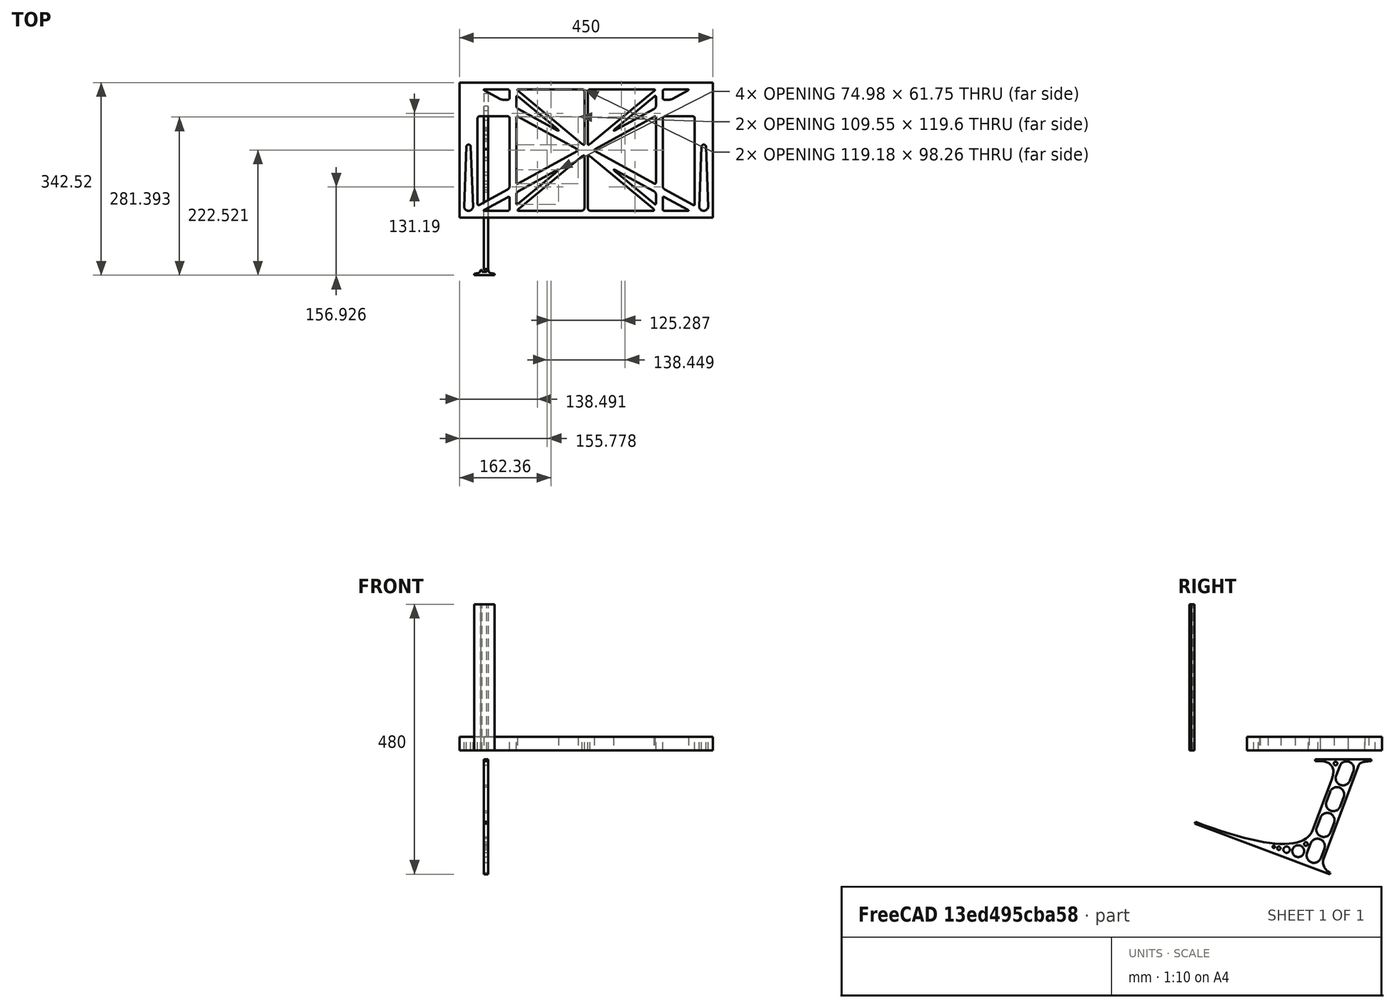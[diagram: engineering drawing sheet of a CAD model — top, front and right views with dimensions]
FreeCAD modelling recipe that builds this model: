
FCSTD DOCUMENT  (FreeCAD 0.19R0.19.2)
Label: laptopStand158FCStd
License: All rights reserved
LicenseURL: http://en.wikipedia.org/wiki/All_rights_reserved
objects: Sketcher::SketchObject×4, Part::Extrusion×3
note: 7 computed .brp shape members not serialized (recipe doc carries the construction recipe); baked Part::Feature solids carry a one-line shape summary decoded from their .brp

FEATURE [Sketcher::SketchObject] Sketch
  FullyConstrained = false
  sketch-geometry (349):
    g0: LineSegment StartX=-10.9272 StartY=-82.7794 StartZ=0 EndX=46.0728 EndY=-51.4823 EndZ=0
    g1: LineSegment StartX=-10.9272 StartY=76.4095 StartZ=0 EndX=-10.9272 EndY=-82.7794 EndZ=0
    g2: LineSegment StartX=46.0728 StartY=76.4095 StartZ=0 EndX=46.0728 EndY=-51.4823 EndZ=0
    g3: LineSegment StartX=-42.9272 StartY=136.221 StartZ=0 EndX=-42.9272 EndY=-103.779 EndZ=0
    g4: LineSegment StartX=407.073 StartY=136.221 StartZ=0 EndX=407.073 EndY=-103.779 EndZ=0
    g5: ArcOfCircle CenterX=-26.9272 CenterY=-83.7794 CenterZ=0 NormalX=0 NormalY=0 NormalZ=1 AngleXU=0 Radius=8 StartAngle=3.14159 EndAngle=6.28319
    g6: ArcOfCircle CenterX=391.073 CenterY=22.1087 CenterZ=0 NormalX=0 NormalY=0 NormalZ=1 AngleXU=0 Radius=8 StartAngle=-4.4e-15 EndAngle=3.14159
    g7: LineSegment StartX=399.073 StartY=22.1087 StartZ=0 EndX=399.073 EndY=-83.7794 EndZ=0
    g8: LineSegment StartX=383.073 StartY=22.1087 StartZ=0 EndX=383.073 EndY=-83.7794 EndZ=0
    g9: ArcOfCircle CenterX=391.073 CenterY=-83.7794 CenterZ=0 NormalX=0 NormalY=0 NormalZ=1 AngleXU=0 Radius=8 StartAngle=3.14159 EndAngle=6.28319
    g10: Circle CenterX=175.022 CenterY=27.0628 CenterZ=0 NormalX=0 NormalY=0 NormalZ=1 AngleXU=0 Radius=1
    g11: Circle CenterX=179.022 CenterY=24.8665 CenterZ=0 NormalX=0 NormalY=0 NormalZ=1 AngleXU=0 Radius=1
    g12: Circle CenterX=179.022 CenterY=27.0628 CenterZ=0 NormalX=0 NormalY=0 NormalZ=1 AngleXU=0 Radius=1
    g13: BSplineCurve PolesCount=3 KnotsCount=2 Degree=2 IsPeriodic=0
    g14: GeomPoint X=175.022 Y=27.0628 Z=0
    g15: GeomPoint X=179.022 Y=27.0628 Z=0
    g16: Circle CenterX=189.124 CenterY=27.0628 CenterZ=0 NormalX=0 NormalY=0 NormalZ=1 AngleXU=0 Radius=1
    g17: Circle CenterX=185.124 CenterY=24.8665 CenterZ=0 NormalX=0 NormalY=0 NormalZ=1 AngleXU=0 Radius=1
    g18: Circle CenterX=185.124 CenterY=27.0628 CenterZ=0 NormalX=0 NormalY=0 NormalZ=1 AngleXU=0 Radius=1
    g19: BSplineCurve PolesCount=3 KnotsCount=2 Degree=2 IsPeriodic=0
    g20: GeomPoint X=189.124 Y=27.0628 Z=0
    g21: GeomPoint X=185.124 Y=27.0628 Z=0
    g22: Circle CenterX=175.022 CenterY=5.37834 CenterZ=0 NormalX=0 NormalY=0 NormalZ=1 AngleXU=0 Radius=1
    g23: Circle CenterX=179.022 CenterY=7.57463 CenterZ=0 NormalX=0 NormalY=0 NormalZ=1 AngleXU=0 Radius=1
    g24: Circle CenterX=179.022 CenterY=5.34704 CenterZ=0 NormalX=0 NormalY=0 NormalZ=1 AngleXU=0 Radius=1
    g25: BSplineCurve PolesCount=3 KnotsCount=2 Degree=2 IsPeriodic=0
    g26: GeomPoint X=175.022 Y=5.37834 Z=0
    g27: GeomPoint X=179.022 Y=5.34704 Z=0
    g28: Circle CenterX=189.124 CenterY=5.37834 CenterZ=0 NormalX=0 NormalY=0 NormalZ=1 AngleXU=0 Radius=1
    g29: Circle CenterX=185.124 CenterY=7.57463 CenterZ=0 NormalX=0 NormalY=0 NormalZ=1 AngleXU=0 Radius=1
    g30: Circle CenterX=185.124 CenterY=5.34704 CenterZ=0 NormalX=0 NormalY=0 NormalZ=1 AngleXU=0 Radius=1
    g31: BSplineCurve PolesCount=3 KnotsCount=2 Degree=2 IsPeriodic=0
    g32: GeomPoint X=189.124 Y=5.37834 Z=0
    g33: GeomPoint X=185.124 Y=5.34704 Z=0
    g34: Circle CenterX=165.871 CenterY=18.1458 CenterZ=0 NormalX=0 NormalY=0 NormalZ=1 AngleXU=0 Radius=1
    g35: Circle CenterX=169.377 CenterY=16.2206 CenterZ=0 NormalX=0 NormalY=0 NormalZ=1 AngleXU=0 Radius=1
    g36: Circle CenterX=165.871 CenterY=14.2954 CenterZ=0 NormalX=0 NormalY=0 NormalZ=1 AngleXU=0 Radius=1
    g37: BSplineCurve PolesCount=3 KnotsCount=2 Degree=2 IsPeriodic=0
    g38: GeomPoint X=165.871 Y=18.1458 Z=0
    g39: GeomPoint X=165.871 Y=14.2954 Z=0
    g40: Circle CenterX=198.275 CenterY=18.1458 CenterZ=0 NormalX=0 NormalY=0 NormalZ=1 AngleXU=0 Radius=1
    g41: Circle CenterX=194.768 CenterY=16.2206 CenterZ=0 NormalX=0 NormalY=0 NormalZ=1 AngleXU=0 Radius=1
    g42: Circle CenterX=198.275 CenterY=14.2954 CenterZ=0 NormalX=0 NormalY=0 NormalZ=1 AngleXU=0 Radius=1
    g43: BSplineCurve PolesCount=3 KnotsCount=2 Degree=2 IsPeriodic=0
    g44: GeomPoint X=198.275 Y=18.1458 Z=0
    g45: GeomPoint X=198.275 Y=14.2954 Z=0
    g46: LineSegment StartX=407.073 StartY=-103.779 StartZ=0 EndX=-42.9272 EndY=-103.779 EndZ=0
    g47: LineSegment StartX=407.073 StartY=136.221 StartZ=0 EndX=-42.9272 EndY=136.221 EndZ=0
    g48: LineSegment StartX=46.0728 StartY=76.4095 StartZ=0 EndX=-10.9272 EndY=76.4095 EndZ=0
    g49: Circle CenterX=125.607 CenterY=54.1951 CenterZ=0 NormalX=0 NormalY=0 NormalZ=1 AngleXU=0 Radius=1
    g50: Circle CenterX=139.632 CenterY=46.4944 CenterZ=0 NormalX=0 NormalY=0 NormalZ=1 AngleXU=0 Radius=1
    g51: Circle CenterX=127.326 CenterY=56.7187 CenterZ=0 NormalX=0 NormalY=0 NormalZ=1 AngleXU=0 Radius=1
    g52: BSplineCurve PolesCount=3 KnotsCount=2 Degree=2 IsPeriodic=0
    g53: GeomPoint X=125.607 Y=54.1951 Z=0
    g54: GeomPoint X=127.326 Y=56.7187 Z=0
    g55: Circle CenterX=236.821 CenterY=56.7187 CenterZ=0 NormalX=0 NormalY=0 NormalZ=1 AngleXU=0 Radius=1
    g56: Circle CenterX=224.513 CenterY=46.4944 CenterZ=0 NormalX=0 NormalY=0 NormalZ=1 AngleXU=0 Radius=1
    g57: Circle CenterX=238.538 CenterY=54.1951 CenterZ=0 NormalX=0 NormalY=0 NormalZ=1 AngleXU=0 Radius=1
    g58: BSplineCurve PolesCount=3 KnotsCount=2 Degree=2 IsPeriodic=0
    g59: GeomPoint X=236.821 Y=56.7187 Z=0
    g60: GeomPoint X=238.538 Y=54.1951 Z=0
    g61: Circle CenterX=238.538 CenterY=-21.7539 CenterZ=0 NormalX=0 NormalY=0 NormalZ=1 AngleXU=0 Radius=1
    g62: Circle CenterX=224.513 CenterY=-14.0532 CenterZ=0 NormalX=0 NormalY=0 NormalZ=1 AngleXU=0 Radius=1
    g63: Circle CenterX=236.821 CenterY=-24.2775 CenterZ=0 NormalX=0 NormalY=0 NormalZ=1 AngleXU=0 Radius=1
    g64: BSplineCurve PolesCount=3 KnotsCount=2 Degree=2 IsPeriodic=0
    g65: GeomPoint X=238.538 Y=-21.7539 Z=0
    g66: GeomPoint X=236.821 Y=-24.2775 Z=0
    g67: Circle CenterX=125.607 CenterY=-21.7539 CenterZ=0 NormalX=0 NormalY=0 NormalZ=1 AngleXU=0 Radius=1
    g68: Circle CenterX=139.632 CenterY=-14.0532 CenterZ=0 NormalX=0 NormalY=0 NormalZ=1 AngleXU=0 Radius=1
    g69: Circle CenterX=127.325 CenterY=-24.2775 CenterZ=0 NormalX=0 NormalY=0 NormalZ=1 AngleXU=0 Radius=1
    g70: BSplineCurve PolesCount=3 KnotsCount=2 Degree=2 IsPeriodic=0
    g71: GeomPoint X=125.607 Y=-21.7539 Z=0
    g72: GeomPoint X=127.325 Y=-24.2775 Z=0
    g73: Circle CenterX=302.996 CenterY=111.695 CenterZ=0 NormalX=0 NormalY=0 NormalZ=1 AngleXU=0 Radius=1
    g74: Circle CenterX=306.073 CenterY=114.251 CenterZ=0 NormalX=0 NormalY=0 NormalZ=1 AngleXU=0 Radius=1
    g75: Circle CenterX=306.073 CenterY=110.251 CenterZ=0 NormalX=0 NormalY=0 NormalZ=1 AngleXU=0 Radius=1
    g76: BSplineCurve PolesCount=3 KnotsCount=2 Degree=2 IsPeriodic=0
    g77: GeomPoint X=302.996 Y=111.695 Z=0
    g78: GeomPoint X=306.073 Y=110.251 Z=0
    g79: Circle CenterX=306.073 CenterY=95.2763 CenterZ=0 NormalX=0 NormalY=0 NormalZ=1 AngleXU=0 Radius=1
    g80: Circle CenterX=306.073 CenterY=91.2763 CenterZ=0 NormalX=0 NormalY=0 NormalZ=1 AngleXU=0 Radius=1
    g81: Circle CenterX=302.567 CenterY=89.3511 CenterZ=0 NormalX=0 NormalY=0 NormalZ=1 AngleXU=0 Radius=1
    g82: BSplineCurve PolesCount=3 KnotsCount=2 Degree=2 IsPeriodic=0
    g83: GeomPoint X=306.073 Y=95.2763 Z=0
    g84: GeomPoint X=302.567 Y=89.3511 Z=0
    g85: LineSegment StartX=306.073 StartY=110.251 StartZ=0 EndX=306.073 EndY=95.2763 EndZ=0
    g86: LineSegment StartX=302.996 StartY=111.695 StartZ=0 EndX=236.821 EndY=56.7187 EndZ=0
    g87: LineSegment StartX=238.538 StartY=54.1951 StartZ=0 EndX=302.567 EndY=89.3511 EndZ=0
    g88: Circle CenterX=61.1496 CenterY=111.695 CenterZ=0 NormalX=0 NormalY=0 NormalZ=1 AngleXU=0 Radius=1
    g89: Circle CenterX=58.0728 CenterY=114.251 CenterZ=0 NormalX=0 NormalY=0 NormalZ=1 AngleXU=0 Radius=1
    g90: Circle CenterX=58.0728 CenterY=110.251 CenterZ=0 NormalX=0 NormalY=0 NormalZ=1 AngleXU=0 Radius=1
    g91: BSplineCurve PolesCount=3 KnotsCount=2 Degree=2 IsPeriodic=0
    g92: GeomPoint X=61.1496 Y=111.695 Z=0
    g93: GeomPoint X=58.0728 Y=110.251 Z=0
    g94: Circle CenterX=61.5791 CenterY=89.3511 CenterZ=0 NormalX=0 NormalY=0 NormalZ=1 AngleXU=0 Radius=1
    g95: Circle CenterX=58.0728 CenterY=91.2763 CenterZ=0 NormalX=0 NormalY=0 NormalZ=1 AngleXU=0 Radius=1
    g96: Circle CenterX=58.0728 CenterY=95.2763 CenterZ=0 NormalX=0 NormalY=0 NormalZ=1 AngleXU=0 Radius=1
    g97: BSplineCurve PolesCount=3 KnotsCount=2 Degree=2 IsPeriodic=0
    g98: GeomPoint X=61.5791 Y=89.3511 Z=0
    g99: GeomPoint X=58.0728 Y=95.2763 Z=0
    g100: LineSegment StartX=58.0728 StartY=110.251 StartZ=0 EndX=58.0728 EndY=95.2763 EndZ=0
    g101: LineSegment StartX=61.1496 StartY=111.695 StartZ=0 EndX=127.326 EndY=56.7187 EndZ=0
    g102: LineSegment StartX=125.607 StartY=54.1951 StartZ=0 EndX=61.5791 EndY=89.3511 EndZ=0
    g103: Circle CenterX=61.5791 CenterY=-56.9099 CenterZ=0 NormalX=0 NormalY=0 NormalZ=1 AngleXU=0 Radius=1
    g104: Circle CenterX=58.0728 CenterY=-58.8351 CenterZ=0 NormalX=0 NormalY=0 NormalZ=1 AngleXU=0 Radius=1
    g105: Circle CenterX=58.0728 CenterY=-62.8351 CenterZ=0 NormalX=0 NormalY=0 NormalZ=1 AngleXU=0 Radius=1
    g106: BSplineCurve PolesCount=3 KnotsCount=2 Degree=2 IsPeriodic=0
    g107: GeomPoint X=61.5791 Y=-56.9099 Z=0
    g108: GeomPoint X=58.0728 Y=-62.8351 Z=0
    g109: Circle CenterX=58.0728 CenterY=-77.8102 CenterZ=0 NormalX=0 NormalY=0 NormalZ=1 AngleXU=0 Radius=1
    g110: Circle CenterX=58.0728 CenterY=-81.8102 CenterZ=0 NormalX=0 NormalY=0 NormalZ=1 AngleXU=0 Radius=1
    g111: Circle CenterX=61.1496 CenterY=-79.2541 CenterZ=0 NormalX=0 NormalY=0 NormalZ=1 AngleXU=0 Radius=1
    g112: BSplineCurve PolesCount=3 KnotsCount=2 Degree=2 IsPeriodic=0
    g113: GeomPoint X=58.0728 Y=-77.8102 Z=0
    g114: GeomPoint X=61.1496 Y=-79.2541 Z=0
    g115: LineSegment StartX=58.0728 StartY=-62.8351 StartZ=0 EndX=58.0728 EndY=-77.8102 EndZ=0
    g116: LineSegment StartX=61.1496 StartY=-79.2541 StartZ=0 EndX=127.325 EndY=-24.2775 EndZ=0
    g117: LineSegment StartX=125.607 StartY=-21.7539 StartZ=0 EndX=61.5791 EndY=-56.9099 EndZ=0
    g118: Circle CenterX=302.567 CenterY=-56.9099 CenterZ=0 NormalX=0 NormalY=0 NormalZ=1 AngleXU=0 Radius=1
    g119: Circle CenterX=306.073 CenterY=-58.8351 CenterZ=0 NormalX=0 NormalY=0 NormalZ=1 AngleXU=0 Radius=1
    g120: Circle CenterX=306.073 CenterY=-62.8351 CenterZ=0 NormalX=0 NormalY=0 NormalZ=1 AngleXU=0 Radius=1
    g121: BSplineCurve PolesCount=3 KnotsCount=2 Degree=2 IsPeriodic=0
    g122: GeomPoint X=302.567 Y=-56.9099 Z=0
    g123: GeomPoint X=306.073 Y=-62.8351 Z=0
    g124: Circle CenterX=302.996 CenterY=-79.2541 CenterZ=0 NormalX=0 NormalY=0 NormalZ=1 AngleXU=0 Radius=1
    g125: Circle CenterX=306.073 CenterY=-81.8102 CenterZ=0 NormalX=0 NormalY=0 NormalZ=1 AngleXU=0 Radius=1
    g126: Circle CenterX=306.073 CenterY=-77.8102 CenterZ=0 NormalX=0 NormalY=0 NormalZ=1 AngleXU=0 Radius=1
    g127: BSplineCurve PolesCount=3 KnotsCount=2 Degree=2 IsPeriodic=0
    g128: GeomPoint X=302.996 Y=-79.2541 Z=0
    g129: GeomPoint X=306.073 Y=-77.8102 Z=0
    g130: LineSegment StartX=306.073 StartY=-62.8351 StartZ=0 EndX=306.073 EndY=-77.8102 EndZ=0
    g131: LineSegment StartX=302.996 StartY=-79.2541 StartZ=0 EndX=236.821 EndY=-24.2775 EndZ=0
    g132: LineSegment StartX=238.538 StartY=-21.7539 StartZ=0 EndX=302.567 EndY=-56.9099 EndZ=0
    g133: Circle CenterX=61.6457 CenterY=-88.8112 CenterZ=0 NormalX=0 NormalY=0 NormalZ=1 AngleXU=0 Radius=1
    g134: Circle CenterX=58.0728 CenterY=-91.7794 CenterZ=0 NormalX=0 NormalY=0 NormalZ=1 AngleXU=0 Radius=1
    g135: Circle CenterX=63.9135 CenterY=-91.7794 CenterZ=0 NormalX=0 NormalY=0 NormalZ=1 AngleXU=0 Radius=1
    g136: BSplineCurve PolesCount=3 KnotsCount=2 Degree=2 IsPeriodic=0
    g137: GeomPoint X=61.6457 Y=-88.8112 Z=0
    g138: GeomPoint X=63.9135 Y=-91.7794 Z=0
    g139: Circle CenterX=179.022 CenterY=-85.8163 CenterZ=0 NormalX=0 NormalY=0 NormalZ=1 AngleXU=0 Radius=1
    g140: Circle CenterX=179.022 CenterY=-91.7794 CenterZ=0 NormalX=0 NormalY=0 NormalZ=1 AngleXU=0 Radius=1
    g141: Circle CenterX=171.895 CenterY=-91.7794 CenterZ=0 NormalX=0 NormalY=0 NormalZ=1 AngleXU=0 Radius=1
    g142: BSplineCurve PolesCount=3 KnotsCount=2 Degree=2 IsPeriodic=0
    g143: GeomPoint X=179.022 Y=-85.8163 Z=0
    g144: GeomPoint X=171.895 Y=-91.7794 Z=0
    g145: Circle CenterX=185.124 CenterY=-86.2028 CenterZ=0 NormalX=0 NormalY=0 NormalZ=1 AngleXU=0 Radius=1
    g146: Circle CenterX=185.124 CenterY=-91.7794 CenterZ=0 NormalX=0 NormalY=0 NormalZ=1 AngleXU=0 Radius=1
    g147: Circle CenterX=191.747 CenterY=-91.7794 CenterZ=0 NormalX=0 NormalY=0 NormalZ=1 AngleXU=0 Radius=1
    g148: BSplineCurve PolesCount=3 KnotsCount=2 Degree=2 IsPeriodic=0
    g149: GeomPoint X=185.124 Y=-86.2028 Z=0
    g150: GeomPoint X=191.747 Y=-91.7794 Z=0
    g151: Circle CenterX=299.888 CenterY=-86.6413 CenterZ=0 NormalX=0 NormalY=0 NormalZ=1 AngleXU=0 Radius=1
    g152: Circle CenterX=306.073 CenterY=-91.7794 CenterZ=0 NormalX=0 NormalY=0 NormalZ=1 AngleXU=0 Radius=1
    g153: Circle CenterX=298.776 CenterY=-91.7794 CenterZ=0 NormalX=0 NormalY=0 NormalZ=1 AngleXU=0 Radius=1
    g154: BSplineCurve PolesCount=3 KnotsCount=2 Degree=2 IsPeriodic=0
    g155: GeomPoint X=299.888 Y=-86.6413 Z=0
    g156: GeomPoint X=298.776 Y=-91.7794 Z=0
    g157: LineSegment StartX=189.124 StartY=5.37834 StartZ=0 EndX=299.888 EndY=-86.6413 EndZ=0
    g158: LineSegment StartX=298.776 StartY=-91.7794 StartZ=0 EndX=191.747 EndY=-91.7794 EndZ=0
    g159: LineSegment StartX=185.124 StartY=-86.2028 StartZ=0 EndX=185.124 EndY=5.34704 EndZ=0
    g160: LineSegment StartX=179.022 StartY=5.34704 StartZ=0 EndX=179.022 EndY=-85.8163 EndZ=0
    g161: LineSegment StartX=171.895 StartY=-91.7794 StartZ=0 EndX=63.9135 EndY=-91.7794 EndZ=0
    g162: LineSegment StartX=61.6457 StartY=-88.8112 StartZ=0 EndX=175.022 EndY=5.37834 EndZ=0
    g163: Circle CenterX=302.073 CenterY=124.221 CenterZ=0 NormalX=0 NormalY=0 NormalZ=1 AngleXU=0 Radius=1
    g164: Circle CenterX=306.073 CenterY=124.221 CenterZ=0 NormalX=0 NormalY=0 NormalZ=1 AngleXU=0 Radius=1
    g165: Circle CenterX=302.996 CenterY=121.665 CenterZ=0 NormalX=0 NormalY=0 NormalZ=1 AngleXU=0 Radius=1
    g166: BSplineCurve PolesCount=3 KnotsCount=2 Degree=2 IsPeriodic=0
    g167: GeomPoint X=302.073 Y=124.221 Z=0
    g168: GeomPoint X=302.996 Y=121.665 Z=0
    g169: Circle CenterX=189.124 CenterY=124.221 CenterZ=0 NormalX=0 NormalY=0 NormalZ=1 AngleXU=0 Radius=1
    g170: Circle CenterX=185.124 CenterY=124.221 CenterZ=0 NormalX=0 NormalY=0 NormalZ=1 AngleXU=0 Radius=1
    g171: Circle CenterX=185.124 CenterY=120.221 CenterZ=0 NormalX=0 NormalY=0 NormalZ=1 AngleXU=0 Radius=1
    g172: BSplineCurve PolesCount=3 KnotsCount=2 Degree=2 IsPeriodic=0
    g173: GeomPoint X=189.124 Y=124.221 Z=0
    g174: GeomPoint X=185.124 Y=120.221 Z=0
    g175: Circle CenterX=175.022 CenterY=124.221 CenterZ=0 NormalX=0 NormalY=0 NormalZ=1 AngleXU=0 Radius=1
    g176: Circle CenterX=179.022 CenterY=124.221 CenterZ=0 NormalX=0 NormalY=0 NormalZ=1 AngleXU=0 Radius=1
    g177: Circle CenterX=179.022 CenterY=120.221 CenterZ=0 NormalX=0 NormalY=0 NormalZ=1 AngleXU=0 Radius=1
    g178: BSplineCurve PolesCount=3 KnotsCount=2 Degree=2 IsPeriodic=0
    g179: GeomPoint X=175.022 Y=124.221 Z=0
    g180: GeomPoint X=179.022 Y=120.221 Z=0
    g181: Circle CenterX=62.0728 CenterY=124.221 CenterZ=0 NormalX=0 NormalY=0 NormalZ=1 AngleXU=0 Radius=1
    g182: Circle CenterX=58.0728 CenterY=124.221 CenterZ=0 NormalX=0 NormalY=0 NormalZ=1 AngleXU=0 Radius=1
    g183: Circle CenterX=61.1496 CenterY=121.665 CenterZ=0 NormalX=0 NormalY=0 NormalZ=1 AngleXU=0 Radius=1
    g184: BSplineCurve PolesCount=3 KnotsCount=2 Degree=2 IsPeriodic=0
    g185: GeomPoint X=62.0728 Y=124.221 Z=0
    g186: GeomPoint X=61.1496 Y=121.665 Z=0
    g187: LineSegment StartX=62.0728 StartY=124.221 StartZ=0 EndX=175.022 EndY=124.221 EndZ=0
    g188: LineSegment StartX=179.022 StartY=120.221 StartZ=0 EndX=179.022 EndY=27.0628 EndZ=0
    g189: LineSegment StartX=185.124 StartY=27.0628 StartZ=0 EndX=185.124 EndY=120.221 EndZ=0
    g190: LineSegment StartX=189.124 StartY=124.221 StartZ=0 EndX=302.073 EndY=124.221 EndZ=0
    g191: LineSegment StartX=302.996 StartY=121.665 StartZ=0 EndX=189.124 EndY=27.0628 EndZ=0
    g192: LineSegment StartX=175.022 StartY=27.0628 StartZ=0 EndX=61.1496 EndY=121.665 EndZ=0
    g193: Circle CenterX=61.5791 CenterY=75.4095 CenterZ=0 NormalX=0 NormalY=0 NormalZ=1 AngleXU=0 Radius=1
    g194: Circle CenterX=58.0728 CenterY=77.3346 CenterZ=0 NormalX=0 NormalY=0 NormalZ=1 AngleXU=0 Radius=1
    g195: Circle CenterX=58.0728 CenterY=73.3346 CenterZ=0 NormalX=0 NormalY=0 NormalZ=1 AngleXU=0 Radius=1
    g196: BSplineCurve PolesCount=3 KnotsCount=2 Degree=2 IsPeriodic=0
    g197: GeomPoint X=61.5791 Y=75.4095 Z=0
    g198: GeomPoint X=58.0728 Y=73.3346 Z=0
    g199: Circle CenterX=58.0728 CenterY=-40.8935 CenterZ=0 NormalX=0 NormalY=0 NormalZ=1 AngleXU=0 Radius=1
    g200: Circle CenterX=58.0728 CenterY=-44.8935 CenterZ=0 NormalX=0 NormalY=0 NormalZ=1 AngleXU=0 Radius=1
    g201: Circle CenterX=61.5791 CenterY=-42.9683 CenterZ=0 NormalX=0 NormalY=0 NormalZ=1 AngleXU=0 Radius=1
    g202: BSplineCurve PolesCount=3 KnotsCount=2 Degree=2 IsPeriodic=0
    g203: GeomPoint X=58.0728 Y=-40.8935 Z=0
    g204: GeomPoint X=61.5791 Y=-42.9683 Z=0
    g205: LineSegment StartX=61.5791 StartY=-42.9683 StartZ=0 EndX=165.871 EndY=14.2954 EndZ=0
    g206: LineSegment StartX=165.871 StartY=18.1458 StartZ=0 EndX=61.5791 EndY=75.4095 EndZ=0
    g207: LineSegment StartX=58.0728 StartY=73.3346 StartZ=0 EndX=58.0728 EndY=-40.8935 EndZ=0
    g208: Circle CenterX=302.567 CenterY=-42.9683 CenterZ=0 NormalX=0 NormalY=0 NormalZ=1 AngleXU=0 Radius=1
    g209: Circle CenterX=306.073 CenterY=-44.8935 CenterZ=0 NormalX=0 NormalY=0 NormalZ=1 AngleXU=0 Radius=1
    g210: Circle CenterX=306.073 CenterY=-40.8935 CenterZ=0 NormalX=0 NormalY=0 NormalZ=1 AngleXU=0 Radius=1
    g211: BSplineCurve PolesCount=3 KnotsCount=2 Degree=2 IsPeriodic=0
    g212: GeomPoint X=302.567 Y=-42.9683 Z=0
    g213: GeomPoint X=306.073 Y=-40.8935 Z=0
    g214: Circle CenterX=306.073 CenterY=73.3346 CenterZ=0 NormalX=0 NormalY=0 NormalZ=1 AngleXU=0 Radius=1
    g215: Circle CenterX=306.073 CenterY=77.3346 CenterZ=0 NormalX=0 NormalY=0 NormalZ=1 AngleXU=0 Radius=1
    g216: Circle CenterX=302.567 CenterY=75.4095 CenterZ=0 NormalX=0 NormalY=0 NormalZ=1 AngleXU=0 Radius=1
    g217: BSplineCurve PolesCount=3 KnotsCount=2 Degree=2 IsPeriodic=0
    g218: GeomPoint X=306.073 Y=73.3346 Z=0
    g219: GeomPoint X=302.567 Y=75.4095 Z=0
    g220: LineSegment StartX=302.567 StartY=-42.9683 StartZ=0 EndX=198.275 EndY=14.2954 EndZ=0
    g221: LineSegment StartX=198.275 StartY=18.1458 StartZ=0 EndX=302.567 EndY=75.4095 EndZ=0
    g222: LineSegment StartX=306.073 StartY=73.3346 StartZ=0 EndX=306.073 EndY=-40.8935 EndZ=0
    g223: LineSegment StartX=322.073 StartY=105.865 StartZ=0 EndX=328.643 EndY=105.865 EndZ=0
    g224: LineSegment StartX=318.073 StartY=120.221 StartZ=0 EndX=318.073 EndY=109.865 EndZ=0
    g225: LineSegment StartX=336.157 StartY=107.779 StartZ=0 EndX=362.567 EndY=122.294 EndZ=0
    g226: Circle CenterX=362.073 CenterY=124.221 CenterZ=0 NormalX=0 NormalY=0 NormalZ=1 AngleXU=0 Radius=1
    g227: Circle CenterX=366.073 CenterY=124.221 CenterZ=0 NormalX=0 NormalY=0 NormalZ=1 AngleXU=0 Radius=1
    g228: Circle CenterX=362.567 CenterY=122.294 CenterZ=0 NormalX=0 NormalY=0 NormalZ=1 AngleXU=0 Radius=1
    g229: BSplineCurve PolesCount=3 KnotsCount=2 Degree=2 IsPeriodic=0
    g230: GeomPoint X=362.073 Y=124.221 Z=0
    g231: GeomPoint X=362.567 Y=122.294 Z=0
    g232: Circle CenterX=322.073 CenterY=124.221 CenterZ=0 NormalX=0 NormalY=0 NormalZ=1 AngleXU=0 Radius=1
    g233: Circle CenterX=318.073 CenterY=124.221 CenterZ=0 NormalX=0 NormalY=0 NormalZ=1 AngleXU=0 Radius=1
    g234: Circle CenterX=318.073 CenterY=120.221 CenterZ=0 NormalX=0 NormalY=0 NormalZ=1 AngleXU=0 Radius=1
    g235: BSplineCurve PolesCount=3 KnotsCount=2 Degree=2 IsPeriodic=0
    g236: GeomPoint X=322.073 Y=124.221 Z=0
    g237: GeomPoint X=318.073 Y=120.221 Z=0
    g238: Circle CenterX=322.073 CenterY=105.865 CenterZ=0 NormalX=0 NormalY=0 NormalZ=1 AngleXU=0 Radius=1
    g239: Circle CenterX=318.073 CenterY=105.865 CenterZ=0 NormalX=0 NormalY=0 NormalZ=1 AngleXU=0 Radius=1
    g240: Circle CenterX=318.073 CenterY=109.865 CenterZ=0 NormalX=0 NormalY=0 NormalZ=1 AngleXU=0 Radius=1
    g241: BSplineCurve PolesCount=3 KnotsCount=2 Degree=2 IsPeriodic=0
    g242: GeomPoint X=322.073 Y=105.865 Z=0
    g243: GeomPoint X=318.073 Y=109.865 Z=0
    g244: Circle CenterX=336.157 CenterY=107.779 CenterZ=0 NormalX=0 NormalY=0 NormalZ=1 AngleXU=0 Radius=1
    g245: Circle CenterX=332.651 CenterY=105.853 CenterZ=0 NormalX=0 NormalY=0 NormalZ=1 AngleXU=0 Radius=1
    g246: Circle CenterX=328.643 CenterY=105.865 CenterZ=0 NormalX=0 NormalY=0 NormalZ=1 AngleXU=0 Radius=1
    g247: BSplineCurve PolesCount=3 KnotsCount=2 Degree=2 IsPeriodic=0
    g248: GeomPoint X=336.157 Y=107.779 Z=0
    g249: GeomPoint X=328.643 Y=105.865 Z=0
    g250: LineSegment StartX=322.073 StartY=124.221 StartZ=0 EndX=362.073 EndY=124.221 EndZ=0
    g251: Circle CenterX=371.567 CenterY=-80.8644 CenterZ=0 NormalX=0 NormalY=0 NormalZ=1 AngleXU=0 Radius=1
    g252: Circle CenterX=375.073 CenterY=-82.7896 CenterZ=0 NormalX=0 NormalY=0 NormalZ=1 AngleXU=0 Radius=1
    g253: Circle CenterX=375.073 CenterY=-78.7896 CenterZ=0 NormalX=0 NormalY=0 NormalZ=1 AngleXU=0 Radius=1
    g254: BSplineCurve PolesCount=3 KnotsCount=2 Degree=2 IsPeriodic=0
    g255: GeomPoint X=371.567 Y=-80.8644 Z=0
    g256: GeomPoint X=375.073 Y=-78.7896 Z=0
    g257: Circle CenterX=321.579 CenterY=-53.4075 CenterZ=0 NormalX=0 NormalY=0 NormalZ=1 AngleXU=0 Radius=1
    g258: Circle CenterX=318.073 CenterY=-51.4823 CenterZ=0 NormalX=0 NormalY=0 NormalZ=1 AngleXU=0 Radius=1
    g259: Circle CenterX=318.073 CenterY=-47.4805 CenterZ=0 NormalX=0 NormalY=0 NormalZ=1 AngleXU=0 Radius=1
    g260: BSplineCurve PolesCount=3 KnotsCount=2 Degree=2 IsPeriodic=0
    g261: GeomPoint X=321.579 Y=-53.4075 Z=0
    g262: GeomPoint X=318.073 Y=-47.4805 Z=0
    g263: LineSegment StartX=371.567 StartY=-80.8644 StartZ=0 EndX=321.579 EndY=-53.4075 EndZ=0
    g264: Circle CenterX=321.579 CenterY=-67.3492 CenterZ=0 NormalX=0 NormalY=0 NormalZ=1 AngleXU=0 Radius=1
    g265: Circle CenterX=318.073 CenterY=-65.424 CenterZ=0 NormalX=0 NormalY=0 NormalZ=1 AngleXU=0 Radius=1
    g266: Circle CenterX=318.073 CenterY=-69.424 CenterZ=0 NormalX=0 NormalY=0 NormalZ=1 AngleXU=0 Radius=1
    g267: BSplineCurve PolesCount=3 KnotsCount=2 Degree=2 IsPeriodic=0
    g268: GeomPoint X=321.579 Y=-67.3492 Z=0
    g269: GeomPoint X=318.073 Y=-69.424 Z=0
    g270: Circle CenterX=362.567 CenterY=-89.8542 CenterZ=0 NormalX=0 NormalY=0 NormalZ=1 AngleXU=0 Radius=1
    g271: Circle CenterX=366.073 CenterY=-91.7794 CenterZ=0 NormalX=0 NormalY=0 NormalZ=1 AngleXU=0 Radius=1
    g272: Circle CenterX=362.073 CenterY=-91.7794 CenterZ=0 NormalX=0 NormalY=0 NormalZ=1 AngleXU=0 Radius=1
    g273: BSplineCurve PolesCount=3 KnotsCount=2 Degree=2 IsPeriodic=0
    g274: GeomPoint X=362.567 Y=-89.8542 Z=0
    g275: GeomPoint X=362.073 Y=-91.7794 Z=0
    g276: Circle CenterX=322.073 CenterY=-91.7794 CenterZ=0 NormalX=0 NormalY=0 NormalZ=1 AngleXU=0 Radius=1
    g277: Circle CenterX=318.073 CenterY=-91.7794 CenterZ=0 NormalX=0 NormalY=0 NormalZ=1 AngleXU=0 Radius=1
    g278: Circle CenterX=318.073 CenterY=-87.7794 CenterZ=0 NormalX=0 NormalY=0 NormalZ=1 AngleXU=0 Radius=1
    g279: BSplineCurve PolesCount=3 KnotsCount=2 Degree=2 IsPeriodic=0
    g280: GeomPoint X=322.073 Y=-91.7794 Z=0
    g281: GeomPoint X=318.073 Y=-87.7794 Z=0
    g282: LineSegment StartX=362.567 StartY=-89.8542 StartZ=0 EndX=321.579 EndY=-67.3492 EndZ=0
    g283: LineSegment StartX=318.073 StartY=-69.424 StartZ=0 EndX=318.073 EndY=-87.7794 EndZ=0
    g284: LineSegment StartX=322.073 StartY=-91.7794 StartZ=0 EndX=362.073 EndY=-91.7794 EndZ=0
    g285: Circle CenterX=2.07281 CenterY=124.221 CenterZ=0 NormalX=0 NormalY=0 NormalZ=1 AngleXU=0 Radius=1
    g286: Circle CenterX=1.57905 CenterY=122.295 CenterZ=0 NormalX=0 NormalY=0 NormalZ=1 AngleXU=0 Radius=1
    g287: BSplineCurve PolesCount=3 KnotsCount=2 Degree=2 IsPeriodic=0
    g288: GeomPoint X=2.07281 Y=124.221 Z=0
    g289: GeomPoint X=1.57905 Y=122.295 Z=0
    g290: Circle CenterX=42.0728 CenterY=124.221 CenterZ=0 NormalX=0 NormalY=0 NormalZ=1 AngleXU=0 Radius=1
    g291: Circle CenterX=46.0728 CenterY=124.221 CenterZ=0 NormalX=0 NormalY=0 NormalZ=1 AngleXU=0 Radius=1
    g292: Circle CenterX=46.0728 CenterY=120.221 CenterZ=0 NormalX=0 NormalY=0 NormalZ=1 AngleXU=0 Radius=1
    g293: BSplineCurve PolesCount=3 KnotsCount=2 Degree=2 IsPeriodic=0
    g294: GeomPoint X=42.0728 Y=124.221 Z=0
    g295: GeomPoint X=46.0728 Y=120.221 Z=0
    g296: Circle CenterX=46.0728 CenterY=109.865 CenterZ=0 NormalX=0 NormalY=0 NormalZ=1 AngleXU=0 Radius=1
    g297: Circle CenterX=46.0728 CenterY=105.865 CenterZ=0 NormalX=0 NormalY=0 NormalZ=1 AngleXU=0 Radius=1
    g298: Circle CenterX=42.0728 CenterY=105.865 CenterZ=0 NormalX=0 NormalY=0 NormalZ=1 AngleXU=0 Radius=1
    g299: BSplineCurve PolesCount=3 KnotsCount=2 Degree=2 IsPeriodic=0
    g300: GeomPoint X=46.0728 Y=109.865 Z=0
    g301: GeomPoint X=42.0728 Y=105.865 Z=0
    g302: Circle CenterX=35.5028 CenterY=105.865 CenterZ=0 NormalX=0 NormalY=0 NormalZ=1 AngleXU=0 Radius=1
    g303: Circle CenterX=31.5028 CenterY=105.865 CenterZ=0 NormalX=0 NormalY=0 NormalZ=1 AngleXU=0 Radius=1
    g304: Circle CenterX=27.9965 CenterY=107.79 CenterZ=0 NormalX=0 NormalY=0 NormalZ=1 AngleXU=0 Radius=1
    g305: BSplineCurve PolesCount=3 KnotsCount=2 Degree=2 IsPeriodic=0
    g306: GeomPoint X=35.5028 Y=105.865 Z=0
    g307: GeomPoint X=27.9965 Y=107.79 Z=0
    g308: LineSegment StartX=2.07281 StartY=124.221 StartZ=0 EndX=42.0728 EndY=124.221 EndZ=0
    g309: LineSegment StartX=46.0728 StartY=120.221 StartZ=0 EndX=46.0728 EndY=109.865 EndZ=0
    g310: LineSegment StartX=42.0728 StartY=105.865 StartZ=0 EndX=35.5028 EndY=105.865 EndZ=0
    g311: LineSegment StartX=27.9965 StartY=107.79 StartZ=0 EndX=1.57905 EndY=122.295 EndZ=0
    g312: Circle CenterX=42.5666 CenterY=-67.3492 CenterZ=0 NormalX=0 NormalY=0 NormalZ=1 AngleXU=0 Radius=1
    g313: Circle CenterX=46.0728 CenterY=-65.424 CenterZ=0 NormalX=0 NormalY=0 NormalZ=1 AngleXU=0 Radius=1
    g314: Circle CenterX=46.0728 CenterY=-69.424 CenterZ=0 NormalX=0 NormalY=0 NormalZ=1 AngleXU=0 Radius=1
    g315: BSplineCurve PolesCount=3 KnotsCount=2 Degree=2 IsPeriodic=0
    g316: GeomPoint X=42.5666 Y=-67.3492 Z=0
    g317: GeomPoint X=46.0728 Y=-69.424 Z=0
    g318: Circle CenterX=46.0728 CenterY=-87.7794 CenterZ=0 NormalX=0 NormalY=0 NormalZ=1 AngleXU=0 Radius=1
    g319: Circle CenterX=46.0728 CenterY=-91.7794 CenterZ=0 NormalX=0 NormalY=0 NormalZ=1 AngleXU=0 Radius=1
    g320: Circle CenterX=42.0728 CenterY=-91.7794 CenterZ=0 NormalX=0 NormalY=0 NormalZ=1 AngleXU=0 Radius=1
    g321: BSplineCurve PolesCount=3 KnotsCount=2 Degree=2 IsPeriodic=0
    g322: GeomPoint X=46.0728 Y=-87.7794 Z=0
    g323: GeomPoint X=42.0728 Y=-91.7794 Z=0
    g324: Circle CenterX=2.07281 CenterY=-91.7794 CenterZ=0 NormalX=0 NormalY=0 NormalZ=1 AngleXU=0 Radius=1
    g325: Circle CenterX=-1.92719 CenterY=-91.7794 CenterZ=0 NormalX=0 NormalY=0 NormalZ=1 AngleXU=0 Radius=1
    g326: Circle CenterX=1.57905 CenterY=-89.8542 CenterZ=0 NormalX=0 NormalY=0 NormalZ=1 AngleXU=0 Radius=1
    g327: BSplineCurve PolesCount=3 KnotsCount=2 Degree=2 IsPeriodic=0
    g328: GeomPoint X=2.07281 Y=-91.7794 Z=0
    g329: GeomPoint X=1.57905 Y=-89.8542 Z=0
    g330: LineSegment StartX=2.07281 StartY=-91.7794 StartZ=0 EndX=42.0728 EndY=-91.7794 EndZ=0
    g331: LineSegment StartX=46.0728 StartY=-87.7794 StartZ=0 EndX=46.0728 EndY=-69.424 EndZ=0
    g332: LineSegment StartX=42.5666 StartY=-67.3492 StartZ=0 EndX=1.57905 EndY=-89.8542 EndZ=0
    g333: Circle CenterX=322.073 CenterY=76.4095 CenterZ=0 NormalX=0 NormalY=0 NormalZ=1 AngleXU=0 Radius=4
    g334: BSplineCurve PolesCount=3 KnotsCount=2 Degree=2 IsPeriodic=0
    g335: GeomPoint X=318.073 Y=72.4095 Z=0
    g336: GeomPoint X=322.073 Y=76.4095 Z=0
    g337: Circle CenterX=375.073 CenterY=72.4095 CenterZ=0 NormalX=0 NormalY=0 NormalZ=1 AngleXU=0 Radius=1
    g338: Circle CenterX=375.073 CenterY=76.4095 CenterZ=0 NormalX=0 NormalY=0 NormalZ=1 AngleXU=0 Radius=1
    g339: Circle CenterX=371.073 CenterY=76.4095 CenterZ=0 NormalX=0 NormalY=0 NormalZ=1 AngleXU=0 Radius=1
    g340: BSplineCurve PolesCount=3 KnotsCount=2 Degree=2 IsPeriodic=0
    g341: GeomPoint X=375.073 Y=72.4095 Z=0
    g342: GeomPoint X=371.073 Y=76.4095 Z=0
    g343: LineSegment StartX=322.073 StartY=76.4095 StartZ=0 EndX=371.073 EndY=76.4095 EndZ=0
    g344: LineSegment StartX=318.073 StartY=72.4095 StartZ=0 EndX=318.073 EndY=-47.4805 EndZ=0
    g345: LineSegment StartX=375.073 StartY=72.4095 StartZ=0 EndX=375.073 EndY=-78.7896 EndZ=0
    g346: ArcOfCircle CenterX=-26.9272 CenterY=22.1087 CenterZ=0 NormalX=0 NormalY=0 NormalZ=1 AngleXU=0 Radius=4 StartAngle=5e-16 EndAngle=3.14159
    g347: LineSegment StartX=-30.9272 StartY=22.1087 StartZ=0 EndX=-34.9272 EndY=-83.7794 EndZ=0
    g348: LineSegment StartX=-18.9272 StartY=-83.7794 StartZ=0 EndX=-22.9272 EndY=22.1087 EndZ=0
  constraints (572):
    c: Coincident(g0,g2)
    c: Block(g0)
    c: Block(g1)
    c: Vertical(g3)
    c: Vertical(g4)
    c: Block(g4)
    c: Block(g3)
    c: Tangent(g6,g7) = 1.5708
    c: Tangent(g7,g9) = 1.5708
    c: Equal(g6,g9)
    c: Coincident(g8,g6)
    c: Coincident(g8,g9)
    c: Block(g7)
    c: Block(g8)
    c: Weight(g10) = 1
    c: Equal(g10,g11)
    c: Equal(g10,g12)
    c: InternalAlignment(g10,g13)
    c: InternalAlignment(g11,g13)
    c: InternalAlignment(g12,g13)
    c: InternalAlignment(g14,g13)
    c: InternalAlignment(g15,g13)
    c: Weight(g16) = 1
    c: Equal(g16,g17)
    c: Equal(g16,g18)
    c: InternalAlignment(g16,g19)
    c: InternalAlignment(g17,g19)
    c: InternalAlignment(g18,g19)
    c: InternalAlignment(g20,g19)
    c: InternalAlignment(g21,g19)
    c: Block(g19)
    c: Block(g13)
    c: Weight(g22) = 1
    c: Equal(g22,g23)
    c: Equal(g22,g24)
    c: InternalAlignment(g22,g25)
    c: InternalAlignment(g23,g25)
    c: InternalAlignment(g24,g25)
    c: InternalAlignment(g26,g25)
    c: InternalAlignment(g27,g25)
    c: Weight(g28) = 1
    c: Equal(g28,g29)
    c: Equal(g28,g30)
    c: InternalAlignment(g28,g31)
    c: InternalAlignment(g29,g31)
    c: InternalAlignment(g30,g31)
    c: InternalAlignment(g32,g31)
    c: InternalAlignment(g33,g31)
    c: Block(g31)
    c: Block(g25)
    c: Weight(g34) = 1
    c: Equal(g34,g35)
    c: Equal(g34,g36)
    c: InternalAlignment(g34,g37)
    c: InternalAlignment(g35,g37)
    c: InternalAlignment(g36,g37)
    c: InternalAlignment(g38,g37)
    c: InternalAlignment(g39,g37)
    c: Weight(g40) = 1
    c: Equal(g40,g41)
    c: Equal(g40,g42)
    c: InternalAlignment(g40,g43)
    c: InternalAlignment(g41,g43)
    c: InternalAlignment(g42,g43)
    c: InternalAlignment(g44,g43)
    c: InternalAlignment(g45,g43)
    c: Block(g37)
    c: Block(g43)
    c: Coincident(g46,g4)
    c: Coincident(g46,g3)
    c: Horizontal(g46)
    c: Distance(g46) = 450
    c: Coincident(g47,g4)
    c: Coincident(g47,g3)
    c: Horizontal(g47)
    c: Horizontal(g48)
    c: Coincident(g2,g48)
    c: Block(g48)
    c: Coincident(g1,g48)
    c: Weight(g49) = 1
    c: Equal(g49,g50)
    c: Equal(g49,g51)
    c: InternalAlignment(g49,g52)
    c: InternalAlignment(g50,g52)
    c: InternalAlignment(g51,g52)
    c: InternalAlignment(g53,g52)
    c: InternalAlignment(g54,g52)
    c: Block(g52)
    c: Weight(g55) = 1
    c: Equal(g55,g56)
    c: Equal(g55,g57)
    c: InternalAlignment(g55,g58)
    c: InternalAlignment(g56,g58)
    c: InternalAlignment(g57,g58)
    c: InternalAlignment(g59,g58)
    c: InternalAlignment(g60,g58)
    c: Block(g58)
    c: Weight(g61) = 1
    c: Equal(g61,g62)
    c: Equal(g61,g63)
    c: InternalAlignment(g61,g64)
    c: InternalAlignment(g62,g64)
    c: InternalAlignment(g63,g64)
    c: InternalAlignment(g65,g64)
    c: InternalAlignment(g66,g64)
    c: Block(g64)
    c: Weight(g67) = 1
    c: Equal(g67,g68)
    c: Equal(g67,g69)
    c: InternalAlignment(g67,g70)
    c: InternalAlignment(g68,g70)
    c: InternalAlignment(g69,g70)
    c: InternalAlignment(g71,g70)
    c: InternalAlignment(g72,g70)
    c: Block(g70)
    c: Weight(g73) = 1
    c: Equal(g73,g74)
    c: Equal(g73,g75)
    c: InternalAlignment(g73,g76)
    c: InternalAlignment(g74,g76)
    c: InternalAlignment(g75,g76)
    c: InternalAlignment(g77,g76)
    c: InternalAlignment(g78,g76)
    c: Weight(g79) = 1
    c: Equal(g79,g80)
    c: Equal(g79,g81)
    c: InternalAlignment(g79,g82)
    c: InternalAlignment(g80,g82)
    c: InternalAlignment(g81,g82)
    c: InternalAlignment(g83,g82)
    c: InternalAlignment(g84,g82)
    c: Block(g76)
    c: Block(g82)
    c: Coincident(g85,g76)
    c: Coincident(g85,g82)
    c: Vertical(g85)
    c: Coincident(g86,g76)
    c: Coincident(g86,g58)
    c: Coincident(g87,g58)
    c: Coincident(g87,g82)
    c: Weight(g88) = 1
    c: Equal(g88,g89)
    c: Equal(g88,g90)
    c: InternalAlignment(g88,g91)
    c: InternalAlignment(g89,g91)
    c: InternalAlignment(g90,g91)
    c: InternalAlignment(g92,g91)
    c: InternalAlignment(g93,g91)
    c: Weight(g94) = 1
    c: Equal(g94,g95)
    c: Equal(g94,g96)
    c: InternalAlignment(g94,g97)
    c: InternalAlignment(g95,g97)
    c: InternalAlignment(g96,g97)
    c: InternalAlignment(g98,g97)
    c: InternalAlignment(g99,g97)
    c: Block(g91)
    c: Block(g97)
    c: Coincident(g100,g91)
    c: Coincident(g100,g97)
    c: Vertical(g100)
    c: Coincident(g101,g91)
    c: Coincident(g101,g52)
    c: Coincident(g102,g52)
    c: Coincident(g102,g97)
    c: Weight(g103) = 1
    c: Equal(g103,g104)
    c: Equal(g103,g105)
    c: InternalAlignment(g103,g106)
    c: InternalAlignment(g104,g106)
    c: InternalAlignment(g105,g106)
    c: InternalAlignment(g107,g106)
    c: InternalAlignment(g108,g106)
    c: Weight(g109) = 1
    c: Equal(g109,g110)
    c: Equal(g109,g111)
    c: InternalAlignment(g109,g112)
    c: InternalAlignment(g110,g112)
    c: InternalAlignment(g111,g112)
    c: InternalAlignment(g113,g112)
    c: InternalAlignment(g114,g112)
    c: Block(g106)
    c: Block(g112)
    c: Coincident(g115,g106)
    c: Coincident(g115,g112)
    c: Vertical(g115)
    c: Coincident(g116,g112)
    c: Coincident(g116,g70)
    c: Coincident(g117,g70)
    c: Coincident(g117,g106)
    c: Weight(g118) = 1
    c: Equal(g118,g119)
    c: Equal(g118,g120)
    c: InternalAlignment(g118,g121)
    c: InternalAlignment(g119,g121)
    c: InternalAlignment(g120,g121)
    c: InternalAlignment(g122,g121)
    c: InternalAlignment(g123,g121)
    c: Weight(g124) = 1
    c: Equal(g124,g125)
    c: Equal(g124,g126)
    c: InternalAlignment(g124,g127)
    c: InternalAlignment(g125,g127)
    c: InternalAlignment(g126,g127)
    c: InternalAlignment(g128,g127)
    c: InternalAlignment(g129,g127)
    c: Block(g121)
    c: Block(g127)
    c: Coincident(g130,g121)
    c: Coincident(g130,g127)
    c: Vertical(g130)
    c: Coincident(g131,g127)
    c: Coincident(g131,g64)
    c: Coincident(g132,g64)
    c: Coincident(g132,g121)
    c: Weight(g133) = 1
    c: Equal(g133,g134)
    c: Equal(g133,g135)
    c: InternalAlignment(g133,g136)
    c: InternalAlignment(g134,g136)
    c: InternalAlignment(g135,g136)
    c: InternalAlignment(g137,g136)
    c: InternalAlignment(g138,g136)
    c: Weight(g139) = 1
    c: Equal(g139,g140)
    c: Equal(g139,g141)
    c: InternalAlignment(g139,g142)
    c: InternalAlignment(g140,g142)
    c: InternalAlignment(g141,g142)
    c: InternalAlignment(g143,g142)
    c: InternalAlignment(g144,g142)
    c: Weight(g145) = 1
    c: Equal(g145,g146)
    c: Equal(g145,g147)
    c: InternalAlignment(g145,g148)
    c: InternalAlignment(g146,g148)
    c: InternalAlignment(g147,g148)
    c: InternalAlignment(g149,g148)
    c: InternalAlignment(g150,g148)
    c: Weight(g151) = 1
    c: Equal(g151,g152)
    c: Equal(g151,g153)
    c: InternalAlignment(g151,g154)
    c: InternalAlignment(g152,g154)
    c: InternalAlignment(g153,g154)
    c: InternalAlignment(g155,g154)
    c: InternalAlignment(g156,g154)
    c: Block(g154)
    c: Block(g148)
    c: Block(g142)
    c: Block(g136)
    c: Coincident(g157,g31)
    c: Coincident(g157,g154)
    c: Coincident(g158,g154)
    c: Coincident(g158,g148)
    c: Horizontal(g158)
    c: Coincident(g159,g148)
    c: Coincident(g159,g31)
    c: Vertical(g159)
    c: Coincident(g160,g25)
    c: Coincident(g160,g142)
    c: Vertical(g160)
    c: Coincident(g161,g142)
    c: Coincident(g161,g136)
    c: Horizontal(g161)
    c: Coincident(g162,g136)
    c: Coincident(g162,g25)
    c: Weight(g163) = 1
    c: Equal(g163,g164)
    c: Equal(g163,g165)
    c: InternalAlignment(g163,g166)
    c: InternalAlignment(g164,g166)
    c: InternalAlignment(g165,g166)
    c: InternalAlignment(g167,g166)
    c: InternalAlignment(g168,g166)
    c: Weight(g169) = 1
    c: Equal(g169,g170)
    c: Equal(g169,g171)
    c: InternalAlignment(g169,g172)
    c: InternalAlignment(g170,g172)
    c: InternalAlignment(g171,g172)
    c: InternalAlignment(g173,g172)
    c: InternalAlignment(g174,g172)
    c: Weight(g175) = 1
    c: Equal(g175,g176)
    c: Equal(g175,g177)
    c: InternalAlignment(g175,g178)
    c: InternalAlignment(g176,g178)
    c: InternalAlignment(g177,g178)
    c: InternalAlignment(g179,g178)
    c: InternalAlignment(g180,g178)
    c: Weight(g181) = 1
    c: Equal(g181,g182)
    c: Equal(g181,g183)
    c: InternalAlignment(g181,g184)
    c: InternalAlignment(g182,g184)
    c: InternalAlignment(g183,g184)
    c: InternalAlignment(g185,g184)
    c: InternalAlignment(g186,g184)
    c: Block(g184)
    c: Block(g178)
    c: Block(g172)
    c: Block(g166)
    c: Coincident(g187,g184)
    c: Coincident(g187,g178)
    c: Horizontal(g187)
    c: Coincident(g188,g178)
    c: Coincident(g188,g13)
    c: Vertical(g188)
    c: Coincident(g189,g19)
    c: Coincident(g189,g172)
    c: Vertical(g189)
    c: Coincident(g190,g172)
    c: Coincident(g190,g166)
    c: Horizontal(g190)
    c: Coincident(g191,g166)
    c: Coincident(g191,g19)
    c: Coincident(g192,g13)
    c: Weight(g193) = 1
    c: Equal(g193,g194)
    c: Equal(g193,g195)
    c: InternalAlignment(g193,g196)
    c: InternalAlignment(g194,g196)
    c: InternalAlignment(g195,g196)
    c: InternalAlignment(g197,g196)
    c: InternalAlignment(g198,g196)
    c: Weight(g199) = 1
    c: Equal(g199,g200)
    c: Equal(g199,g201)
    c: InternalAlignment(g199,g202)
    c: InternalAlignment(g200,g202)
    c: InternalAlignment(g201,g202)
    c: InternalAlignment(g203,g202)
    c: InternalAlignment(g204,g202)
    c: Block(g202)
    c: Block(g196)
    c: Coincident(g205,g202)
    c: Coincident(g205,g37)
    c: Coincident(g206,g37)
    c: Coincident(g206,g196)
    c: Coincident(g207,g196)
    c: Coincident(g207,g202)
    c: Vertical(g207)
    c: Weight(g208) = 1
    c: Equal(g208,g209)
    c: Equal(g208,g210)
    c: InternalAlignment(g208,g211)
    c: InternalAlignment(g209,g211)
    c: InternalAlignment(g210,g211)
    c: InternalAlignment(g212,g211)
    c: InternalAlignment(g213,g211)
    c: Weight(g214) = 1
    c: Equal(g214,g215)
    c: Equal(g214,g216)
    c: InternalAlignment(g214,g217)
    c: InternalAlignment(g215,g217)
    c: InternalAlignment(g216,g217)
    c: InternalAlignment(g218,g217)
    c: InternalAlignment(g219,g217)
    c: Block(g217)
    c: Block(g211)
    c: Coincident(g220,g211)
    c: Coincident(g220,g43)
    c: Coincident(g221,g43)
    c: Coincident(g221,g217)
    c: Coincident(g222,g217)
    c: Coincident(g222,g211)
    c: Vertical(g222)
    c: Horizontal(g223)
    c: Block(g223)
    c: Vertical(g224)
    c: Block(g224)
    c: Block(g225)
    c: Weight(g226) = 1
    c: Equal(g226,g227)
    c: Equal(g226,g228)
    c: InternalAlignment(g226,g229)
    c: InternalAlignment(g227,g229)
    c: InternalAlignment(g228,g229)
    c: InternalAlignment(g230,g229)
    c: InternalAlignment(g231,g229)
    c: Weight(g232) = 1
    c: Equal(g232,g233)
    c: Equal(g232,g234)
    c: InternalAlignment(g232,g235)
    c: InternalAlignment(g233,g235)
    c: InternalAlignment(g234,g235)
    c: InternalAlignment(g236,g235)
    c: InternalAlignment(g237,g235)
    c: Weight(g238) = 1
    c: Equal(g238,g239)
    c: Equal(g238,g240)
    c: InternalAlignment(g238,g241)
    c: InternalAlignment(g239,g241)
    c: InternalAlignment(g240,g241)
    c: InternalAlignment(g242,g241)
    c: InternalAlignment(g243,g241)
    c: Weight(g244) = 1
    c: Equal(g244,g245)
    c: Equal(g244,g246)
    c: InternalAlignment(g244,g247)
    c: InternalAlignment(g245,g247)
    c: InternalAlignment(g246,g247)
    c: InternalAlignment(g248,g247)
    c: InternalAlignment(g249,g247)
    c: Block(g229)
    c: Block(g235)
    c: Block(g241)
    c: Block(g247)
    c: Coincident(g250,g235)
    c: Coincident(g250,g229)
    c: Horizontal(g250)
    c: Block(g192)
    c: Weight(g251) = 1
    c: Equal(g251,g252)
    c: Equal(g251,g253)
    c: InternalAlignment(g251,g254)
    c: InternalAlignment(g252,g254)
    c: InternalAlignment(g253,g254)
    c: InternalAlignment(g255,g254)
    c: InternalAlignment(g256,g254)
    c: Weight(g257) = 1
    c: Equal(g257,g258)
    c: Equal(g257,g259)
    c: InternalAlignment(g257,g260)
    c: InternalAlignment(g258,g260)
    c: InternalAlignment(g259,g260)
    c: InternalAlignment(g261,g260)
    c: InternalAlignment(g262,g260)
    c: Block(g254)
    c: Block(g260)
    c: Coincident(g263,g254)
    c: Coincident(g263,g260)
    c: Weight(g264) = 1
    c: Equal(g264,g265)
    c: Equal(g264,g266)
    c: InternalAlignment(g264,g267)
    c: InternalAlignment(g265,g267)
    c: InternalAlignment(g266,g267)
    c: InternalAlignment(g268,g267)
    c: InternalAlignment(g269,g267)
    c: Weight(g270) = 1
    c: Equal(g270,g271)
    c: Equal(g270,g272)
    c: InternalAlignment(g270,g273)
    c: InternalAlignment(g271,g273)
    c: InternalAlignment(g272,g273)
    c: InternalAlignment(g274,g273)
    c: InternalAlignment(g275,g273)
    c: Weight(g276) = 1
    c: Equal(g276,g277)
    c: Equal(g276,g278)
    c: InternalAlignment(g276,g279)
    c: InternalAlignment(g277,g279)
    c: InternalAlignment(g278,g279)
    c: InternalAlignment(g280,g279)
    c: InternalAlignment(g281,g279)
    c: Block(g279)
    c: Block(g273)
    c: Block(g267)
    c: Coincident(g282,g273)
    c: Coincident(g282,g267)
    c: Coincident(g283,g267)
    c: Coincident(g283,g279)
    c: Vertical(g283)
    c: Coincident(g284,g279)
    c: Coincident(g284,g273)
    c: Horizontal(g284)
    c: Weight(g285) = 1
    c: Equal(g285,g286)
    c: InternalAlignment(g285,g287)
    c: InternalAlignment(g286,g287)
    c: InternalAlignment(g288,g287)
    c: InternalAlignment(g289,g287)
    c: Weight(g290) = 1
    c: InternalAlignment(g291,g293)
    c: InternalAlignment(g292,g293)
    c: InternalAlignment(g294,g293)
    c: InternalAlignment(g295,g293)
    c: Weight(g296) = 1
    c: Equal(g296,g297)
    c: Equal(g296,g298)
    c: InternalAlignment(g296,g299)
    c: InternalAlignment(g297,g299)
    c: InternalAlignment(g298,g299)
    c: InternalAlignment(g300,g299)
    c: InternalAlignment(g301,g299)
    c: Equal(g302,g303)
    c: Equal(g302,g304)
    c: InternalAlignment(g302,g305)
    c: InternalAlignment(g303,g305)
    c: InternalAlignment(g304,g305)
    c: InternalAlignment(g306,g305)
    c: InternalAlignment(g307,g305)
    c: Block(g293)
    c: Block(g299)
    c: Block(g305)
    c: Block(g287)
    c: Coincident(g308,g287)
    c: Coincident(g308,g293)
    c: Horizontal(g308)
    c: Coincident(g309,g293)
    c: Coincident(g309,g299)
    c: Vertical(g309)
    c: Coincident(g310,g299)
    c: Coincident(g310,g305)
    c: Horizontal(g310)
    c: Coincident(g311,g305)
    c: Coincident(g311,g287)
    c: Weight(g312) = 1
    c: Equal(g312,g313)
    c: Equal(g312,g314)
    c: InternalAlignment(g312,g315)
    c: InternalAlignment(g313,g315)
    c: InternalAlignment(g314,g315)
    c: InternalAlignment(g316,g315)
    c: InternalAlignment(g317,g315)
    c: Weight(g318) = 1
    c: Equal(g318,g319)
    c: Equal(g318,g320)
    c: InternalAlignment(g318,g321)
    c: InternalAlignment(g319,g321)
    c: InternalAlignment(g320,g321)
    c: InternalAlignment(g322,g321)
    c: InternalAlignment(g323,g321)
    c: Weight(g324) = 1
    c: Equal(g324,g325)
    c: Equal(g324,g326)
    c: InternalAlignment(g324,g327)
    c: InternalAlignment(g325,g327)
    c: InternalAlignment(g326,g327)
    c: InternalAlignment(g328,g327)
    c: InternalAlignment(g329,g327)
    c: Block(g327)
    c: Block(g321)
    c: Block(g315)
    c: Coincident(g330,g327)
    c: Coincident(g330,g321)
    c: Horizontal(g330)
    c: Coincident(g331,g321)
    c: Coincident(g331,g315)
    c: Vertical(g331)
    c: Coincident(g332,g315)
    c: Coincident(g332,g327)
    c: InternalAlignment(g333,g334)
    c: InternalAlignment(g335,g334)
    c: InternalAlignment(g336,g334)
    c: Block(g334)
    c: Equal(g337,g338)
    c: Equal(g337,g339)
    c: InternalAlignment(g337,g340)
    c: InternalAlignment(g338,g340)
    c: InternalAlignment(g339,g340)
    c: InternalAlignment(g341,g340)
    c: InternalAlignment(g342,g340)
    c: Block(g340)
    c: Coincident(g343,g334)
    c: Horizontal(g343)
    c: Block(g343)
    c: Coincident(g344,g334)
    c: Coincident(g344,g260)
    c: Vertical(g344)
    c: Coincident(g345,g340)
    c: Coincident(g345,g254)
    c: Vertical(g345)
    c: Coincident(g347,g5)
    c: Coincident(g348,g5)
    c: Block(g346)
    c: Block(g5)
    c: Block(g348)
    c: Block(g347)
    c: Distance(g344) = 119.89
FEATURE [Sketcher::SketchObject] Sketch001
  FullyConstrained = true
  MapMode = 4
  Placement = pos=(0,0,0) rot=(0.57735,0.57735,0.57735;2.0944rad)
  Support = -> [Sketch]
  sketch-geometry (46):
    g0: BSplineCurve PolesCount=3 KnotsCount=2 Degree=2 IsPeriodic=0
    g1: ArcOfCircle CenterX=73.1223 CenterY=-32.291 CenterZ=0 NormalX=0 NormalY=0 NormalZ=1 AngleXU=0 Radius=13 StartAngle=5.92268 EndAngle=9.06428
    g2: ArcOfCircle CenterX=66.7816 CenterY=-49.1439 CenterZ=0 NormalX=0 NormalY=0 NormalZ=1 AngleXU=0 Radius=13 StartAngle=2.78068 EndAngle=5.92131
    g3: ArcOfCircle CenterX=55.9263 CenterY=-78.1807 CenterZ=0 NormalX=0 NormalY=0 NormalZ=1 AngleXU=0 Radius=13 StartAngle=5.92268 EndAngle=9.06428
    g4: ArcOfCircle CenterX=49.5884 CenterY=-95.0342 CenterZ=0 NormalX=0 NormalY=0 NormalZ=1 AngleXU=0 Radius=13 StartAngle=2.78068 EndAngle=5.92131
    g5: ArcOfCircle CenterX=38.7206 CenterY=-124.067 CenterZ=0 NormalX=0 NormalY=0 NormalZ=1 AngleXU=0 Radius=13 StartAngle=5.92268 EndAngle=9.06428
    g6: ArcOfCircle CenterX=32.3875 CenterY=-140.92 CenterZ=0 NormalX=0 NormalY=0 NormalZ=1 AngleXU=0 Radius=13 StartAngle=2.78068 EndAngle=5.92131
    g7: ArcOfCircle CenterX=21.4715 CenterY=-169.934 CenterZ=0 NormalX=0 NormalY=0 NormalZ=1 AngleXU=0 Radius=13 StartAngle=5.92268 EndAngle=9.06428
    g8: ArcOfCircle CenterX=15.1336 CenterY=-186.787 CenterZ=0 NormalX=0 NormalY=0 NormalZ=1 AngleXU=0 Radius=13 StartAngle=2.78068 EndAngle=5.92131
    g9-g12: Circle x4 (B-spline internal-alignment scaffolding for g13; pole/knot coordinates omitted)
    g13: BSplineCurve PolesCount=4 KnotsCount=2 Degree=3 IsPeriodic=0
    g14: GeomPoint X=28.8094 Y=-19.0875 Z=0
    g15: GeomPoint X=47.0443 Y=-50.4712 Z=0
    g16: Circle CenterX=53.5586 CenterY=-23.2695 CenterZ=0 NormalX=0 NormalY=0 NormalZ=1 AngleXU=0 Radius=3.24518
    g17: Circle CenterX=-195.441 CenterY=-127.082 CenterZ=0 NormalX=0 NormalY=0 NormalZ=1 AngleXU=0 Radius=1
    g18: Circle CenterX=-8.24091 CenterY=-197.481 CenterZ=0 NormalX=0 NormalY=0 NormalZ=1 AngleXU=0 Radius=1
    g19: Circle CenterX=12.8789 CenterY=-141.321 CenterZ=0 NormalX=0 NormalY=0 NormalZ=1 AngleXU=0 Radius=1
    g20: BSplineCurve PolesCount=3 KnotsCount=2 Degree=2 IsPeriodic=0
    g21: GeomPoint X=-195.441 Y=-127.082 Z=0
    g22: GeomPoint X=12.8789 Y=-141.321 Z=0
    g23: Circle CenterX=-12.8016 CenterY=-179.036 CenterZ=0 NormalX=0 NormalY=0 NormalZ=1 AngleXU=0 Radius=10.5072
    g24: Circle CenterX=0.933922 CenterY=-166.43 CenterZ=0 NormalX=0 NormalY=0 NormalZ=1 AngleXU=0 Radius=3.26661
    g25: Circle CenterX=-33.5518 CenterY=-176.44 CenterZ=0 NormalX=0 NormalY=0 NormalZ=1 AngleXU=0 Radius=5.64388
    g26: Circle CenterX=-47.2366 CenterY=-173.859 CenterZ=0 NormalX=0 NormalY=0 NormalZ=1 AngleXU=0 Radius=3.01653
    g27: Circle CenterX=-56.2595 CenterY=-171.456 CenterZ=0 NormalX=0 NormalY=0 NormalZ=1 AngleXU=0 Radius=2.12826
    g28: ArcOfCircle CenterX=51.2151 CenterY=-198.473 CenterZ=0 NormalX=0 NormalY=0 NormalZ=1 AngleXU=0 Radius=20 StartAngle=2.78189 EndAngle=4.35269
    g29: LineSegment StartX=32.4951 StartY=-191.433 StartZ=0 EndX=94.6578 EndY=-26.1352 EndZ=0
    g30: LineSegment StartX=43.1192 StartY=-220.001 StartZ=0 EndX=-196.497 EndY=-129.89 EndZ=0
    g31: LineSegment StartX=43.1192 StartY=-220.001 StartZ=0 EndX=44.1752 EndY=-217.193 EndZ=0
    g32: LineSegment StartX=117.223 StartY=-19.0875 StartZ=0 EndX=117.223 EndY=-16.0875 EndZ=0
    g33: LineSegment StartX=117.223 StartY=-16.0875 StartZ=0 EndX=17.2232 EndY=-16.0875 EndZ=0
    g34: LineSegment StartX=17.2232 StartY=-16.0875 StartZ=0 EndX=17.2232 EndY=-19.0875 EndZ=0
    g35: LineSegment StartX=28.8094 StartY=-19.0875 StartZ=0 EndX=17.2232 EndY=-19.0875 EndZ=0
    g36: LineSegment StartX=47.0443 StartY=-50.4712 StartZ=0 EndX=12.8789 EndY=-141.321 EndZ=0
    g37: LineSegment StartX=-195.441 StartY=-127.082 StartZ=0 EndX=-196.497 EndY=-129.89 EndZ=0
    g38: LineSegment StartX=85.2866 StartY=-36.8766 StartZ=0 EndX=78.9396 EndY=-53.7463 EndZ=0
    g39: LineSegment StartX=60.9579 StartY=-27.7053 StartZ=0 EndX=54.6191 EndY=-44.5532 EndZ=0
    g40: LineSegment StartX=68.0907 StartY=-82.7664 StartZ=0 EndX=61.7465 EndY=-99.6365 EndZ=0
    g41: LineSegment StartX=43.7619 StartY=-73.595 StartZ=0 EndX=37.426 EndY=-90.4435 EndZ=0
    g42: LineSegment StartX=50.885 StartY=-128.652 StartZ=0 EndX=44.5456 EndY=-145.522 EndZ=0
    g43: LineSegment StartX=26.5562 StartY=-119.481 StartZ=0 EndX=20.2251 EndY=-136.329 EndZ=0
    g44: LineSegment StartX=9.3071 StartY=-165.349 StartZ=0 EndX=2.97115 EndY=-182.197 EndZ=0
    g45: LineSegment StartX=33.6358 StartY=-174.52 StartZ=0 EndX=27.2917 EndY=-191.39 EndZ=0
  constraints (71):
    c: Block(g0)
    c: Block(g1)
    c: Block(g2)
    c: Block(g4)
    c: Block(g3)
    c: Block(g6)
    c: Block(g5)
    c: Block(g8)
    c: Block(g7)
    c: Weight(g9) = 1
    c: Equal(g9,g10)
    c: Equal(g9,g11)
    c: Equal(g9,g12)
    c: InternalAlignment(g9-g12 -> g13) x4
    c: InternalAlignment(g14,g13)
    c: InternalAlignment(g15,g13)
    c: Block(g16)
    c: Weight(g17) = 1
    c: Equal(g17,g18)
    c: Equal(g17,g19)
    c: InternalAlignment(g17,g20)
    c: InternalAlignment(g18,g20)
    c: InternalAlignment(g19,g20)
    c: InternalAlignment(g21,g20)
    c: InternalAlignment(g22,g20)
    c: Block(g20)
    c: Block(g23)
    c: Block(g24)
    c: Block(g25)
    c: Block(g26)
    c: Block(g27)
    c: Block(g28)
    c: Coincident(g29,g28)
    c: Coincident(g29,g0)
    c: Block(g13)
    c: Coincident(g31,g30)
    c: Coincident(g31,g28)
    c: Block(g31)
    c: Coincident(g32,g0)
    c: Vertical(g32)
    c: Coincident(g33,g32)
    c: Horizontal(g33)
    c: Coincident(g34,g33)
    c: Vertical(g34)
    c: Block(g33)
    c: Coincident(g35,g13)
    c: Coincident(g35,g34)
    c: Horizontal(g35)
    c: Coincident(g36,g13)
    c: Coincident(g36,g20)
    c: Coincident(g37,g20)
    c: Coincident(g37,g30)
    c: Block(g30)
    c: Coincident(g38,g1)
    c: Coincident(g38,g2)
    c: Coincident(g39,g1)
    c: Coincident(g39,g2)
    c: Coincident(g40,g3)
    c: Coincident(g40,g4)
    c: Coincident(g41,g3)
    c: Coincident(g41,g4)
    c: Coincident(g42,g5)
    c: Coincident(g42,g6)
    c: Coincident(g43,g5)
    c: Coincident(g43,g6)
    c: Coincident(g44,g7)
    c: Coincident(g44,g8)
    c: Coincident(g45,g7)
    c: Coincident(g45,g8)
    c: Distance(g30) = 256
    c: Distance(g33) = 100
FEATURE [Part::Extrusion] Extrude002
  Base = -> Sketch001
  Dir = (1,0,0)
  DirMode = 2
  FaceMakerClass = Part::FaceMakerBullseye
  LengthFwd = 8
  LengthRev = 0
  Solid = true
  Symmetric = false
FEATURE [Sketcher::SketchObject] Sketch002
  FullyConstrained = true
  sketch-geometry (20):
    g0: LineSegment StartX=-2.77179 StartY=-200.304 StartZ=0 EndX=5.22821 EndY=-200.304 EndZ=0
    g1: LineSegment StartX=5.22821 StartY=-200.304 StartZ=0 EndX=5.22821 EndY=-197.304 EndZ=0
    g2: LineSegment StartX=-2.77179 StartY=-200.304 StartZ=0 EndX=-2.77179 EndY=-197.304 EndZ=0
    g3: LineSegment StartX=5.22821 StartY=-197.304 StartZ=0 EndX=8.22821 EndY=-197.304 EndZ=0
    g4: LineSegment StartX=-2.77179 StartY=-197.304 StartZ=0 EndX=-5.77179 EndY=-197.304 EndZ=0
    g5: LineSegment StartX=19.2282 StartY=-203.304 StartZ=0 EndX=19.2282 EndY=-206.304 EndZ=0
    g6: LineSegment StartX=-16.7718 StartY=-203.304 StartZ=0 EndX=-16.7718 EndY=-206.304 EndZ=0
    g7: LineSegment StartX=-16.7718 StartY=-206.304 StartZ=0 EndX=19.2282 EndY=-206.304 EndZ=0
    g8: Circle CenterX=-16.7718 CenterY=-203.304 CenterZ=0 NormalX=0 NormalY=0 NormalZ=1 AngleXU=0 Radius=1
    g9: Circle CenterX=-5.77179 CenterY=-203.304 CenterZ=0 NormalX=0 NormalY=0 NormalZ=1 AngleXU=0 Radius=1
    g10: Circle CenterX=-5.77179 CenterY=-197.304 CenterZ=0 NormalX=0 NormalY=0 NormalZ=1 AngleXU=0 Radius=1
    g11: BSplineCurve PolesCount=3 KnotsCount=2 Degree=2 IsPeriodic=0
    g12: GeomPoint X=-16.7718 Y=-203.304 Z=0
    g13: GeomPoint X=-5.77179 Y=-197.304 Z=0
    g14: Circle CenterX=19.2282 CenterY=-203.304 CenterZ=0 NormalX=0 NormalY=0 NormalZ=1 AngleXU=0 Radius=1
    g15: Circle CenterX=8.22821 CenterY=-203.304 CenterZ=0 NormalX=0 NormalY=0 NormalZ=1 AngleXU=0 Radius=1
    g16: Circle CenterX=8.22821 CenterY=-197.304 CenterZ=0 NormalX=0 NormalY=0 NormalZ=1 AngleXU=0 Radius=1
    g17: BSplineCurve PolesCount=3 KnotsCount=2 Degree=2 IsPeriodic=0
    g18: GeomPoint X=19.2282 Y=-203.304 Z=0
    g19: GeomPoint X=8.22821 Y=-197.304 Z=0
  constraints (41):
    c: Horizontal(g0)
    c: Distance(g0) = 8
    c: Coincident(g1,g0)
    c: Vertical(g1)
    c: Distance(g1) = 3
    c: Coincident(g2,g0)
    c: Vertical(g2)
    c: Distance(g2) = 3
    c: Coincident(g3,g1)
    c: Horizontal(g3)
    c: Distance(g3) = 3
    c: Coincident(g4,g2)
    c: Horizontal(g4)
    c: Distance(g4) = 3
    c: Vertical(g5)
    c: Vertical(g6)
    c: Coincident(g7,g6)
    c: Coincident(g7,g5)
    c: Weight(g8) = 1
    c: Equal(g8,g9)
    c: Equal(g8,g10)
    c: Coincident(g11,g4)
    c: InternalAlignment(g8,g11)
    c: InternalAlignment(g9,g11)
    c: InternalAlignment(g10,g11)
    c: InternalAlignment(g12,g11)
    c: InternalAlignment(g13,g11)
    c: Coincident(g17,g5)
    c: Weight(g14) = 1
    c: Equal(g14,g15)
    c: Equal(g14,g16)
    c: Coincident(g17,g3)
    c: InternalAlignment(g14,g17)
    c: InternalAlignment(g15,g17)
    c: InternalAlignment(g16,g17)
    c: InternalAlignment(g18,g17)
    c: InternalAlignment(g19,g17)
    c: Block(g7)
    c: Block(g17)
    c: Block(g11)
    c: Block(g6)
FEATURE [Part::Extrusion] Extrude003
  Base = -> Sketch002
  Dir = (0,0,1)
  DirMode = 2
  FaceMakerClass = Part::FaceMakerBullseye
  LengthFwd = 260
  LengthRev = 0
  Solid = true
  Symmetric = false
FEATURE [Sketcher::SketchObject] Sketch003
  FullyConstrained = false
  sketch-geometry (383):
    g0: LineSegment StartX=-42.9272 StartY=136.221 StartZ=0 EndX=-42.9272 EndY=-103.779 EndZ=0
    g1: LineSegment StartX=407.073 StartY=136.221 StartZ=0 EndX=407.073 EndY=-103.779 EndZ=0
    g2: ArcOfCircle CenterX=-26.9272 CenterY=-83.7794 CenterZ=0 NormalX=0 NormalY=0 NormalZ=1 AngleXU=0 Radius=8 StartAngle=3.14159 EndAngle=6.28319
    g3: ArcOfCircle CenterX=391.073 CenterY=-83.7794 CenterZ=0 NormalX=0 NormalY=0 NormalZ=1 AngleXU=0 Radius=8 StartAngle=3.14159 EndAngle=6.28319
    g4: Circle CenterX=175.022 CenterY=27.0628 CenterZ=0 NormalX=0 NormalY=0 NormalZ=1 AngleXU=0 Radius=1
    g5: Circle CenterX=179.022 CenterY=24.8665 CenterZ=0 NormalX=0 NormalY=0 NormalZ=1 AngleXU=0 Radius=1
    g6: Circle CenterX=179.022 CenterY=27.0628 CenterZ=0 NormalX=0 NormalY=0 NormalZ=1 AngleXU=0 Radius=1
    g7: BSplineCurve PolesCount=3 KnotsCount=2 Degree=2 IsPeriodic=0
    g8: GeomPoint X=175.022 Y=27.0628 Z=0
    g9: GeomPoint X=179.022 Y=27.0628 Z=0
    g10: Circle CenterX=189.124 CenterY=27.0628 CenterZ=0 NormalX=0 NormalY=0 NormalZ=1 AngleXU=0 Radius=1
    g11: Circle CenterX=185.124 CenterY=24.8665 CenterZ=0 NormalX=0 NormalY=0 NormalZ=1 AngleXU=0 Radius=1
    g12: Circle CenterX=185.124 CenterY=27.0628 CenterZ=0 NormalX=0 NormalY=0 NormalZ=1 AngleXU=0 Radius=1
    g13: BSplineCurve PolesCount=3 KnotsCount=2 Degree=2 IsPeriodic=0
    g14: GeomPoint X=189.124 Y=27.0628 Z=0
    g15: GeomPoint X=185.124 Y=27.0628 Z=0
    g16: Circle CenterX=175.022 CenterY=5.37834 CenterZ=0 NormalX=0 NormalY=0 NormalZ=1 AngleXU=0 Radius=1
    g17: Circle CenterX=179.022 CenterY=7.57463 CenterZ=0 NormalX=0 NormalY=0 NormalZ=1 AngleXU=0 Radius=1
    g18: Circle CenterX=179.022 CenterY=5.34704 CenterZ=0 NormalX=0 NormalY=0 NormalZ=1 AngleXU=0 Radius=1
    g19: BSplineCurve PolesCount=3 KnotsCount=2 Degree=2 IsPeriodic=0
    g20: GeomPoint X=175.022 Y=5.37834 Z=0
    g21: GeomPoint X=179.022 Y=5.34704 Z=0
    g22: Circle CenterX=189.124 CenterY=5.37834 CenterZ=0 NormalX=0 NormalY=0 NormalZ=1 AngleXU=0 Radius=1
    g23: Circle CenterX=185.124 CenterY=7.57463 CenterZ=0 NormalX=0 NormalY=0 NormalZ=1 AngleXU=0 Radius=1
    g24: Circle CenterX=185.124 CenterY=5.34704 CenterZ=0 NormalX=0 NormalY=0 NormalZ=1 AngleXU=0 Radius=1
    g25: BSplineCurve PolesCount=3 KnotsCount=2 Degree=2 IsPeriodic=0
    g26: GeomPoint X=189.124 Y=5.37834 Z=0
    g27: GeomPoint X=185.124 Y=5.34704 Z=0
    g28: Circle CenterX=165.871 CenterY=18.1458 CenterZ=0 NormalX=0 NormalY=0 NormalZ=1 AngleXU=0 Radius=1
    g29: Circle CenterX=169.377 CenterY=16.2206 CenterZ=0 NormalX=0 NormalY=0 NormalZ=1 AngleXU=0 Radius=1
    g30: Circle CenterX=165.871 CenterY=14.2954 CenterZ=0 NormalX=0 NormalY=0 NormalZ=1 AngleXU=0 Radius=1
    g31: BSplineCurve PolesCount=3 KnotsCount=2 Degree=2 IsPeriodic=0
    g32: GeomPoint X=165.871 Y=18.1458 Z=0
    g33: GeomPoint X=165.871 Y=14.2954 Z=0
    g34: Circle CenterX=198.275 CenterY=18.1458 CenterZ=0 NormalX=0 NormalY=0 NormalZ=1 AngleXU=0 Radius=1
    g35: Circle CenterX=194.768 CenterY=16.2206 CenterZ=0 NormalX=0 NormalY=0 NormalZ=1 AngleXU=0 Radius=1
    g36: Circle CenterX=198.275 CenterY=14.2954 CenterZ=0 NormalX=0 NormalY=0 NormalZ=1 AngleXU=0 Radius=1
    g37: BSplineCurve PolesCount=3 KnotsCount=2 Degree=2 IsPeriodic=0
    g38: GeomPoint X=198.275 Y=18.1458 Z=0
    g39: GeomPoint X=198.275 Y=14.2954 Z=0
    g40: LineSegment StartX=407.073 StartY=-103.779 StartZ=0 EndX=-42.9272 EndY=-103.779 EndZ=0
    g41: Circle CenterX=125.607 CenterY=54.1951 CenterZ=0 NormalX=0 NormalY=0 NormalZ=1 AngleXU=0 Radius=1
    g42: Circle CenterX=139.632 CenterY=46.4944 CenterZ=0 NormalX=0 NormalY=0 NormalZ=1 AngleXU=0 Radius=1
    g43: Circle CenterX=127.326 CenterY=56.7187 CenterZ=0 NormalX=0 NormalY=0 NormalZ=1 AngleXU=0 Radius=1
    g44: BSplineCurve PolesCount=3 KnotsCount=2 Degree=2 IsPeriodic=0
    g45: GeomPoint X=125.607 Y=54.1951 Z=0
    g46: GeomPoint X=127.326 Y=56.7187 Z=0
    g47: Circle CenterX=236.821 CenterY=56.7187 CenterZ=0 NormalX=0 NormalY=0 NormalZ=1 AngleXU=0 Radius=1
    g48: Circle CenterX=224.513 CenterY=46.4944 CenterZ=0 NormalX=0 NormalY=0 NormalZ=1 AngleXU=0 Radius=1
    g49: Circle CenterX=238.538 CenterY=54.1951 CenterZ=0 NormalX=0 NormalY=0 NormalZ=1 AngleXU=0 Radius=1
    g50: BSplineCurve PolesCount=3 KnotsCount=2 Degree=2 IsPeriodic=0
    g51: GeomPoint X=236.821 Y=56.7187 Z=0
    g52: GeomPoint X=238.538 Y=54.1951 Z=0
    g53: Circle CenterX=238.538 CenterY=-21.7539 CenterZ=0 NormalX=0 NormalY=0 NormalZ=1 AngleXU=0 Radius=1
    g54: Circle CenterX=224.513 CenterY=-14.0532 CenterZ=0 NormalX=0 NormalY=0 NormalZ=1 AngleXU=0 Radius=1
    g55: Circle CenterX=236.821 CenterY=-24.2775 CenterZ=0 NormalX=0 NormalY=0 NormalZ=1 AngleXU=0 Radius=1
    g56: BSplineCurve PolesCount=3 KnotsCount=2 Degree=2 IsPeriodic=0
    g57: GeomPoint X=238.538 Y=-21.7539 Z=0
    g58: GeomPoint X=236.821 Y=-24.2775 Z=0
    g59: Circle CenterX=125.607 CenterY=-21.7539 CenterZ=0 NormalX=0 NormalY=0 NormalZ=1 AngleXU=0 Radius=1
    g60: Circle CenterX=139.632 CenterY=-14.0532 CenterZ=0 NormalX=0 NormalY=0 NormalZ=1 AngleXU=0 Radius=1
    g61: Circle CenterX=127.325 CenterY=-24.2775 CenterZ=0 NormalX=0 NormalY=0 NormalZ=1 AngleXU=0 Radius=1
    g62: BSplineCurve PolesCount=3 KnotsCount=2 Degree=2 IsPeriodic=0
    g63: GeomPoint X=125.607 Y=-21.7539 Z=0
    g64: GeomPoint X=127.325 Y=-24.2775 Z=0
    g65: Circle CenterX=302.996 CenterY=111.695 CenterZ=0 NormalX=0 NormalY=0 NormalZ=1 AngleXU=0 Radius=1
    g66: Circle CenterX=306.073 CenterY=114.251 CenterZ=0 NormalX=0 NormalY=0 NormalZ=1 AngleXU=0 Radius=1
    g67: Circle CenterX=306.073 CenterY=110.251 CenterZ=0 NormalX=0 NormalY=0 NormalZ=1 AngleXU=0 Radius=1
    g68: BSplineCurve PolesCount=3 KnotsCount=2 Degree=2 IsPeriodic=0
    g69: GeomPoint X=302.996 Y=111.695 Z=0
    g70: GeomPoint X=306.073 Y=110.251 Z=0
    g71: Circle CenterX=306.073 CenterY=95.2763 CenterZ=0 NormalX=0 NormalY=0 NormalZ=1 AngleXU=0 Radius=1
    g72: Circle CenterX=306.073 CenterY=91.2763 CenterZ=0 NormalX=0 NormalY=0 NormalZ=1 AngleXU=0 Radius=1
    g73: Circle CenterX=302.567 CenterY=89.3511 CenterZ=0 NormalX=0 NormalY=0 NormalZ=1 AngleXU=0 Radius=1
    g74: BSplineCurve PolesCount=3 KnotsCount=2 Degree=2 IsPeriodic=0
    g75: GeomPoint X=306.073 Y=95.2763 Z=0
    g76: GeomPoint X=302.567 Y=89.3511 Z=0
    g77: LineSegment StartX=306.073 StartY=110.251 StartZ=0 EndX=306.073 EndY=95.2763 EndZ=0
    g78: LineSegment StartX=302.996 StartY=111.695 StartZ=0 EndX=236.821 EndY=56.7187 EndZ=0
    g79: LineSegment StartX=238.538 StartY=54.1951 StartZ=0 EndX=302.567 EndY=89.3511 EndZ=0
    g80: Circle CenterX=61.1496 CenterY=111.695 CenterZ=0 NormalX=0 NormalY=0 NormalZ=1 AngleXU=0 Radius=1
    g81: Circle CenterX=58.0728 CenterY=114.251 CenterZ=0 NormalX=0 NormalY=0 NormalZ=1 AngleXU=0 Radius=1
    g82: Circle CenterX=58.0728 CenterY=110.251 CenterZ=0 NormalX=0 NormalY=0 NormalZ=1 AngleXU=0 Radius=1
    g83: BSplineCurve PolesCount=3 KnotsCount=2 Degree=2 IsPeriodic=0
    g84: GeomPoint X=61.1496 Y=111.695 Z=0
    g85: GeomPoint X=58.0728 Y=110.251 Z=0
    g86: Circle CenterX=61.5791 CenterY=89.3511 CenterZ=0 NormalX=0 NormalY=0 NormalZ=1 AngleXU=0 Radius=1
    g87: Circle CenterX=58.0728 CenterY=91.2763 CenterZ=0 NormalX=0 NormalY=0 NormalZ=1 AngleXU=0 Radius=1
    g88: Circle CenterX=58.0728 CenterY=95.2763 CenterZ=0 NormalX=0 NormalY=0 NormalZ=1 AngleXU=0 Radius=1
    g89: BSplineCurve PolesCount=3 KnotsCount=2 Degree=2 IsPeriodic=0
    g90: GeomPoint X=61.5791 Y=89.3511 Z=0
    g91: GeomPoint X=58.0728 Y=95.2763 Z=0
    g92: LineSegment StartX=58.0728 StartY=110.251 StartZ=0 EndX=58.0728 EndY=95.2763 EndZ=0
    g93: LineSegment StartX=61.1496 StartY=111.695 StartZ=0 EndX=127.326 EndY=56.7187 EndZ=0
    g94: LineSegment StartX=125.607 StartY=54.1951 StartZ=0 EndX=61.5791 EndY=89.3511 EndZ=0
    g95: Circle CenterX=61.5791 CenterY=-56.9099 CenterZ=0 NormalX=0 NormalY=0 NormalZ=1 AngleXU=0 Radius=1
    g96: Circle CenterX=58.0728 CenterY=-58.8351 CenterZ=0 NormalX=0 NormalY=0 NormalZ=1 AngleXU=0 Radius=1
    g97: Circle CenterX=58.0728 CenterY=-62.8351 CenterZ=0 NormalX=0 NormalY=0 NormalZ=1 AngleXU=0 Radius=1
    g98: BSplineCurve PolesCount=3 KnotsCount=2 Degree=2 IsPeriodic=0
    g99: GeomPoint X=61.5791 Y=-56.9099 Z=0
    g100: GeomPoint X=58.0728 Y=-62.8351 Z=0
    g101: Circle CenterX=58.0728 CenterY=-77.8102 CenterZ=0 NormalX=0 NormalY=0 NormalZ=1 AngleXU=0 Radius=1
    g102: Circle CenterX=58.0728 CenterY=-81.8102 CenterZ=0 NormalX=0 NormalY=0 NormalZ=1 AngleXU=0 Radius=1
    g103: Circle CenterX=61.1496 CenterY=-79.2541 CenterZ=0 NormalX=0 NormalY=0 NormalZ=1 AngleXU=0 Radius=1
    g104: BSplineCurve PolesCount=3 KnotsCount=2 Degree=2 IsPeriodic=0
    g105: GeomPoint X=58.0728 Y=-77.8102 Z=0
    g106: GeomPoint X=61.1496 Y=-79.2541 Z=0
    g107: LineSegment StartX=58.0728 StartY=-62.8351 StartZ=0 EndX=58.0728 EndY=-77.8102 EndZ=0
    g108: LineSegment StartX=61.1496 StartY=-79.2541 StartZ=0 EndX=127.325 EndY=-24.2775 EndZ=0
    g109: LineSegment StartX=125.607 StartY=-21.7539 StartZ=0 EndX=61.5791 EndY=-56.9099 EndZ=0
    g110: Circle CenterX=302.567 CenterY=-56.9099 CenterZ=0 NormalX=0 NormalY=0 NormalZ=1 AngleXU=0 Radius=1
    g111: Circle CenterX=306.073 CenterY=-58.8351 CenterZ=0 NormalX=0 NormalY=0 NormalZ=1 AngleXU=0 Radius=1
    g112: Circle CenterX=306.073 CenterY=-62.8351 CenterZ=0 NormalX=0 NormalY=0 NormalZ=1 AngleXU=0 Radius=1
    g113: BSplineCurve PolesCount=3 KnotsCount=2 Degree=2 IsPeriodic=0
    g114: GeomPoint X=302.567 Y=-56.9099 Z=0
    g115: GeomPoint X=306.073 Y=-62.8351 Z=0
    g116: Circle CenterX=302.996 CenterY=-79.2541 CenterZ=0 NormalX=0 NormalY=0 NormalZ=1 AngleXU=0 Radius=1
    g117: Circle CenterX=306.073 CenterY=-81.8102 CenterZ=0 NormalX=0 NormalY=0 NormalZ=1 AngleXU=0 Radius=1
    g118: Circle CenterX=306.073 CenterY=-77.8102 CenterZ=0 NormalX=0 NormalY=0 NormalZ=1 AngleXU=0 Radius=1
    g119: BSplineCurve PolesCount=3 KnotsCount=2 Degree=2 IsPeriodic=0
    g120: GeomPoint X=302.996 Y=-79.2541 Z=0
    g121: GeomPoint X=306.073 Y=-77.8102 Z=0
    g122: LineSegment StartX=306.073 StartY=-62.8351 StartZ=0 EndX=306.073 EndY=-77.8102 EndZ=0
    g123: LineSegment StartX=302.996 StartY=-79.2541 StartZ=0 EndX=236.821 EndY=-24.2775 EndZ=0
    g124: LineSegment StartX=238.538 StartY=-21.7539 StartZ=0 EndX=302.567 EndY=-56.9099 EndZ=0
    g125: Circle CenterX=61.6457 CenterY=-88.8112 CenterZ=0 NormalX=0 NormalY=0 NormalZ=1 AngleXU=0 Radius=1
    g126: Circle CenterX=58.0728 CenterY=-91.7794 CenterZ=0 NormalX=0 NormalY=0 NormalZ=1 AngleXU=0 Radius=1
    g127: Circle CenterX=63.9135 CenterY=-91.7794 CenterZ=0 NormalX=0 NormalY=0 NormalZ=1 AngleXU=0 Radius=1
    g128: BSplineCurve PolesCount=3 KnotsCount=2 Degree=2 IsPeriodic=0
    g129: GeomPoint X=61.6457 Y=-88.8112 Z=0
    g130: GeomPoint X=63.9135 Y=-91.7794 Z=0
    g131: Circle CenterX=179.022 CenterY=-85.8163 CenterZ=0 NormalX=0 NormalY=0 NormalZ=1 AngleXU=0 Radius=1
    g132: Circle CenterX=179.022 CenterY=-91.7794 CenterZ=0 NormalX=0 NormalY=0 NormalZ=1 AngleXU=0 Radius=1
    g133: Circle CenterX=171.895 CenterY=-91.7794 CenterZ=0 NormalX=0 NormalY=0 NormalZ=1 AngleXU=0 Radius=1
    g134: BSplineCurve PolesCount=3 KnotsCount=2 Degree=2 IsPeriodic=0
    g135: GeomPoint X=179.022 Y=-85.8163 Z=0
    g136: GeomPoint X=171.895 Y=-91.7794 Z=0
    g137: Circle CenterX=185.124 CenterY=-86.2028 CenterZ=0 NormalX=0 NormalY=0 NormalZ=1 AngleXU=0 Radius=1
    g138: Circle CenterX=185.124 CenterY=-91.7794 CenterZ=0 NormalX=0 NormalY=0 NormalZ=1 AngleXU=0 Radius=1
    g139: Circle CenterX=191.747 CenterY=-91.7794 CenterZ=0 NormalX=0 NormalY=0 NormalZ=1 AngleXU=0 Radius=1
    g140: BSplineCurve PolesCount=3 KnotsCount=2 Degree=2 IsPeriodic=0
    g141: GeomPoint X=185.124 Y=-86.2028 Z=0
    g142: GeomPoint X=191.747 Y=-91.7794 Z=0
    g143: Circle CenterX=299.888 CenterY=-86.6413 CenterZ=0 NormalX=0 NormalY=0 NormalZ=1 AngleXU=0 Radius=1
    g144: Circle CenterX=306.073 CenterY=-91.7794 CenterZ=0 NormalX=0 NormalY=0 NormalZ=1 AngleXU=0 Radius=1
    g145: Circle CenterX=298.776 CenterY=-91.7794 CenterZ=0 NormalX=0 NormalY=0 NormalZ=1 AngleXU=0 Radius=1
    g146: BSplineCurve PolesCount=3 KnotsCount=2 Degree=2 IsPeriodic=0
    g147: GeomPoint X=299.888 Y=-86.6413 Z=0
    g148: GeomPoint X=298.776 Y=-91.7794 Z=0
    g149: LineSegment StartX=189.124 StartY=5.37834 StartZ=0 EndX=299.888 EndY=-86.6413 EndZ=0
    g150: LineSegment StartX=298.776 StartY=-91.7794 StartZ=0 EndX=191.747 EndY=-91.7794 EndZ=0
    g151: LineSegment StartX=185.124 StartY=-86.2028 StartZ=0 EndX=185.124 EndY=5.34704 EndZ=0
    g152: LineSegment StartX=179.022 StartY=5.34704 StartZ=0 EndX=179.022 EndY=-85.8163 EndZ=0
    g153: LineSegment StartX=171.895 StartY=-91.7794 StartZ=0 EndX=63.9135 EndY=-91.7794 EndZ=0
    g154: LineSegment StartX=61.6457 StartY=-88.8112 StartZ=0 EndX=175.022 EndY=5.37834 EndZ=0
    g155: Circle CenterX=302.073 CenterY=124.221 CenterZ=0 NormalX=0 NormalY=0 NormalZ=1 AngleXU=0 Radius=1
    g156: Circle CenterX=306.073 CenterY=124.221 CenterZ=0 NormalX=0 NormalY=0 NormalZ=1 AngleXU=0 Radius=1
    g157: Circle CenterX=302.996 CenterY=121.665 CenterZ=0 NormalX=0 NormalY=0 NormalZ=1 AngleXU=0 Radius=1
    g158: BSplineCurve PolesCount=3 KnotsCount=2 Degree=2 IsPeriodic=0
    g159: GeomPoint X=302.073 Y=124.221 Z=0
    g160: GeomPoint X=302.996 Y=121.665 Z=0
    g161: Circle CenterX=189.124 CenterY=124.221 CenterZ=0 NormalX=0 NormalY=0 NormalZ=1 AngleXU=0 Radius=1
    g162: Circle CenterX=185.124 CenterY=124.221 CenterZ=0 NormalX=0 NormalY=0 NormalZ=1 AngleXU=0 Radius=1
    g163: Circle CenterX=185.124 CenterY=120.221 CenterZ=0 NormalX=0 NormalY=0 NormalZ=1 AngleXU=0 Radius=1
    g164: BSplineCurve PolesCount=3 KnotsCount=2 Degree=2 IsPeriodic=0
    g165: GeomPoint X=189.124 Y=124.221 Z=0
    g166: GeomPoint X=185.124 Y=120.221 Z=0
    g167: Circle CenterX=175.022 CenterY=124.221 CenterZ=0 NormalX=0 NormalY=0 NormalZ=1 AngleXU=0 Radius=1
    g168: Circle CenterX=179.022 CenterY=124.221 CenterZ=0 NormalX=0 NormalY=0 NormalZ=1 AngleXU=0 Radius=1
    g169: Circle CenterX=179.022 CenterY=120.221 CenterZ=0 NormalX=0 NormalY=0 NormalZ=1 AngleXU=0 Radius=1
    g170: BSplineCurve PolesCount=3 KnotsCount=2 Degree=2 IsPeriodic=0
    g171: GeomPoint X=175.022 Y=124.221 Z=0
    g172: GeomPoint X=179.022 Y=120.221 Z=0
    g173: Circle CenterX=62.0728 CenterY=124.221 CenterZ=0 NormalX=0 NormalY=0 NormalZ=1 AngleXU=0 Radius=1
    g174: Circle CenterX=58.0728 CenterY=124.221 CenterZ=0 NormalX=0 NormalY=0 NormalZ=1 AngleXU=0 Radius=1
    g175: Circle CenterX=61.1496 CenterY=121.665 CenterZ=0 NormalX=0 NormalY=0 NormalZ=1 AngleXU=0 Radius=1
    g176: BSplineCurve PolesCount=3 KnotsCount=2 Degree=2 IsPeriodic=0
    g177: GeomPoint X=62.0728 Y=124.221 Z=0
    g178: GeomPoint X=61.1496 Y=121.665 Z=0
    g179: LineSegment StartX=62.0728 StartY=124.221 StartZ=0 EndX=175.022 EndY=124.221 EndZ=0
    g180: LineSegment StartX=179.022 StartY=120.221 StartZ=0 EndX=179.022 EndY=27.0628 EndZ=0
    g181: LineSegment StartX=185.124 StartY=27.0628 StartZ=0 EndX=185.124 EndY=120.221 EndZ=0
    g182: LineSegment StartX=189.124 StartY=124.221 StartZ=0 EndX=302.073 EndY=124.221 EndZ=0
    g183: LineSegment StartX=302.996 StartY=121.665 StartZ=0 EndX=189.124 EndY=27.0628 EndZ=0
    g184: LineSegment StartX=175.022 StartY=27.0628 StartZ=0 EndX=61.1496 EndY=121.665 EndZ=0
    g185: Circle CenterX=61.5791 CenterY=75.4095 CenterZ=0 NormalX=0 NormalY=0 NormalZ=1 AngleXU=0 Radius=1
    g186: Circle CenterX=58.0728 CenterY=77.3346 CenterZ=0 NormalX=0 NormalY=0 NormalZ=1 AngleXU=0 Radius=1
    g187: Circle CenterX=58.0728 CenterY=73.3346 CenterZ=0 NormalX=0 NormalY=0 NormalZ=1 AngleXU=0 Radius=1
    g188: BSplineCurve PolesCount=3 KnotsCount=2 Degree=2 IsPeriodic=0
    g189: GeomPoint X=61.5791 Y=75.4095 Z=0
    g190: GeomPoint X=58.0728 Y=73.3346 Z=0
    g191: Circle CenterX=58.0728 CenterY=-40.8935 CenterZ=0 NormalX=0 NormalY=0 NormalZ=1 AngleXU=0 Radius=1
    g192: Circle CenterX=58.0728 CenterY=-44.8935 CenterZ=0 NormalX=0 NormalY=0 NormalZ=1 AngleXU=0 Radius=1
    g193: Circle CenterX=61.5791 CenterY=-42.9683 CenterZ=0 NormalX=0 NormalY=0 NormalZ=1 AngleXU=0 Radius=1
    g194: BSplineCurve PolesCount=3 KnotsCount=2 Degree=2 IsPeriodic=0
    g195: GeomPoint X=58.0728 Y=-40.8935 Z=0
    g196: GeomPoint X=61.5791 Y=-42.9683 Z=0
    g197: LineSegment StartX=61.5791 StartY=-42.9683 StartZ=0 EndX=165.871 EndY=14.2954 EndZ=0
    g198: LineSegment StartX=165.871 StartY=18.1458 StartZ=0 EndX=61.5791 EndY=75.4095 EndZ=0
    g199: LineSegment StartX=58.0728 StartY=73.3346 StartZ=0 EndX=58.0728 EndY=-40.8935 EndZ=0
    g200: Circle CenterX=302.567 CenterY=-42.9683 CenterZ=0 NormalX=0 NormalY=0 NormalZ=1 AngleXU=0 Radius=1
    g201: Circle CenterX=306.073 CenterY=-44.8935 CenterZ=0 NormalX=0 NormalY=0 NormalZ=1 AngleXU=0 Radius=1
    g202: Circle CenterX=306.073 CenterY=-40.8935 CenterZ=0 NormalX=0 NormalY=0 NormalZ=1 AngleXU=0 Radius=1
    g203: BSplineCurve PolesCount=3 KnotsCount=2 Degree=2 IsPeriodic=0
    g204: GeomPoint X=302.567 Y=-42.9683 Z=0
    g205: GeomPoint X=306.073 Y=-40.8935 Z=0
    g206: Circle CenterX=306.073 CenterY=73.3346 CenterZ=0 NormalX=0 NormalY=0 NormalZ=1 AngleXU=0 Radius=1
    g207: Circle CenterX=306.073 CenterY=77.3346 CenterZ=0 NormalX=0 NormalY=0 NormalZ=1 AngleXU=0 Radius=1
    g208: Circle CenterX=302.567 CenterY=75.4095 CenterZ=0 NormalX=0 NormalY=0 NormalZ=1 AngleXU=0 Radius=1
    g209: BSplineCurve PolesCount=3 KnotsCount=2 Degree=2 IsPeriodic=0
    g210: GeomPoint X=306.073 Y=73.3346 Z=0
    g211: GeomPoint X=302.567 Y=75.4095 Z=0
    g212: LineSegment StartX=302.567 StartY=-42.9683 StartZ=0 EndX=198.275 EndY=14.2954 EndZ=0
    g213: LineSegment StartX=198.275 StartY=18.1458 StartZ=0 EndX=302.567 EndY=75.4095 EndZ=0
    g214: LineSegment StartX=306.073 StartY=73.3346 StartZ=0 EndX=306.073 EndY=-40.8935 EndZ=0
    g215: LineSegment StartX=322.073 StartY=105.865 StartZ=0 EndX=328.643 EndY=105.865 EndZ=0
    g216: LineSegment StartX=318.073 StartY=120.221 StartZ=0 EndX=318.073 EndY=109.865 EndZ=0
    g217: LineSegment StartX=336.157 StartY=107.779 StartZ=0 EndX=362.567 EndY=122.294 EndZ=0
    g218: Circle CenterX=362.073 CenterY=124.221 CenterZ=0 NormalX=0 NormalY=0 NormalZ=1 AngleXU=0 Radius=1
    g219: Circle CenterX=366.073 CenterY=124.221 CenterZ=0 NormalX=0 NormalY=0 NormalZ=1 AngleXU=0 Radius=1
    g220: Circle CenterX=362.567 CenterY=122.294 CenterZ=0 NormalX=0 NormalY=0 NormalZ=1 AngleXU=0 Radius=1
    g221: BSplineCurve PolesCount=3 KnotsCount=2 Degree=2 IsPeriodic=0
    g222: GeomPoint X=362.073 Y=124.221 Z=0
    g223: GeomPoint X=362.567 Y=122.294 Z=0
    g224: Circle CenterX=322.073 CenterY=124.221 CenterZ=0 NormalX=0 NormalY=0 NormalZ=1 AngleXU=0 Radius=1
    g225: Circle CenterX=318.073 CenterY=124.221 CenterZ=0 NormalX=0 NormalY=0 NormalZ=1 AngleXU=0 Radius=1
    g226: Circle CenterX=318.073 CenterY=120.221 CenterZ=0 NormalX=0 NormalY=0 NormalZ=1 AngleXU=0 Radius=1
    g227: BSplineCurve PolesCount=3 KnotsCount=2 Degree=2 IsPeriodic=0
    g228: GeomPoint X=322.073 Y=124.221 Z=0
    g229: GeomPoint X=318.073 Y=120.221 Z=0
    g230: Circle CenterX=322.073 CenterY=105.865 CenterZ=0 NormalX=0 NormalY=0 NormalZ=1 AngleXU=0 Radius=1
    g231: Circle CenterX=318.073 CenterY=105.865 CenterZ=0 NormalX=0 NormalY=0 NormalZ=1 AngleXU=0 Radius=1
    g232: Circle CenterX=318.073 CenterY=109.865 CenterZ=0 NormalX=0 NormalY=0 NormalZ=1 AngleXU=0 Radius=1
    g233: BSplineCurve PolesCount=3 KnotsCount=2 Degree=2 IsPeriodic=0
    g234: GeomPoint X=322.073 Y=105.865 Z=0
    g235: GeomPoint X=318.073 Y=109.865 Z=0
    g236: Circle CenterX=336.157 CenterY=107.779 CenterZ=0 NormalX=0 NormalY=0 NormalZ=1 AngleXU=0 Radius=1
    g237: Circle CenterX=332.651 CenterY=105.853 CenterZ=0 NormalX=0 NormalY=0 NormalZ=1 AngleXU=0 Radius=1
    g238: Circle CenterX=328.643 CenterY=105.865 CenterZ=0 NormalX=0 NormalY=0 NormalZ=1 AngleXU=0 Radius=1
    g239: BSplineCurve PolesCount=3 KnotsCount=2 Degree=2 IsPeriodic=0
    g240: GeomPoint X=336.157 Y=107.779 Z=0
    g241: GeomPoint X=328.643 Y=105.865 Z=0
    g242: LineSegment StartX=322.073 StartY=124.221 StartZ=0 EndX=362.073 EndY=124.221 EndZ=0
    g243: Circle CenterX=371.567 CenterY=-80.8644 CenterZ=0 NormalX=0 NormalY=0 NormalZ=1 AngleXU=0 Radius=1
    g244: Circle CenterX=375.073 CenterY=-82.7896 CenterZ=0 NormalX=0 NormalY=0 NormalZ=1 AngleXU=0 Radius=1
    g245: Circle CenterX=375.073 CenterY=-78.7896 CenterZ=0 NormalX=0 NormalY=0 NormalZ=1 AngleXU=0 Radius=1
    g246: BSplineCurve PolesCount=3 KnotsCount=2 Degree=2 IsPeriodic=0
    g247: GeomPoint X=371.567 Y=-80.8644 Z=0
    g248: GeomPoint X=375.073 Y=-78.7896 Z=0
    g249: Circle CenterX=321.579 CenterY=-53.4075 CenterZ=0 NormalX=0 NormalY=0 NormalZ=1 AngleXU=0 Radius=1
    g250: Circle CenterX=318.073 CenterY=-51.4823 CenterZ=0 NormalX=0 NormalY=0 NormalZ=1 AngleXU=0 Radius=1
    g251: Circle CenterX=318.073 CenterY=-47.4805 CenterZ=0 NormalX=0 NormalY=0 NormalZ=1 AngleXU=0 Radius=1
    g252: BSplineCurve PolesCount=3 KnotsCount=2 Degree=2 IsPeriodic=0
    g253: GeomPoint X=321.579 Y=-53.4075 Z=0
    g254: GeomPoint X=318.073 Y=-47.4805 Z=0
    g255: LineSegment StartX=371.567 StartY=-80.8644 StartZ=0 EndX=321.579 EndY=-53.4075 EndZ=0
    g256: Circle CenterX=321.579 CenterY=-67.3492 CenterZ=0 NormalX=0 NormalY=0 NormalZ=1 AngleXU=0 Radius=1
    g257: Circle CenterX=318.073 CenterY=-65.424 CenterZ=0 NormalX=0 NormalY=0 NormalZ=1 AngleXU=0 Radius=1
    g258: Circle CenterX=318.073 CenterY=-69.424 CenterZ=0 NormalX=0 NormalY=0 NormalZ=1 AngleXU=0 Radius=1
    g259: BSplineCurve PolesCount=3 KnotsCount=2 Degree=2 IsPeriodic=0
    g260: GeomPoint X=321.579 Y=-67.3492 Z=0
    g261: GeomPoint X=318.073 Y=-69.424 Z=0
    g262: Circle CenterX=362.567 CenterY=-89.8542 CenterZ=0 NormalX=0 NormalY=0 NormalZ=1 AngleXU=0 Radius=1
    g263: Circle CenterX=366.073 CenterY=-91.7794 CenterZ=0 NormalX=0 NormalY=0 NormalZ=1 AngleXU=0 Radius=1
    g264: Circle CenterX=362.073 CenterY=-91.7794 CenterZ=0 NormalX=0 NormalY=0 NormalZ=1 AngleXU=0 Radius=1
    g265: BSplineCurve PolesCount=3 KnotsCount=2 Degree=2 IsPeriodic=0
    g266: GeomPoint X=362.567 Y=-89.8542 Z=0
    g267: GeomPoint X=362.073 Y=-91.7794 Z=0
    g268: Circle CenterX=322.073 CenterY=-91.7794 CenterZ=0 NormalX=0 NormalY=0 NormalZ=1 AngleXU=0 Radius=1
    g269: Circle CenterX=318.073 CenterY=-91.7794 CenterZ=0 NormalX=0 NormalY=0 NormalZ=1 AngleXU=0 Radius=1
    g270: Circle CenterX=318.073 CenterY=-87.7794 CenterZ=0 NormalX=0 NormalY=0 NormalZ=1 AngleXU=0 Radius=1
    g271: BSplineCurve PolesCount=3 KnotsCount=2 Degree=2 IsPeriodic=0
    g272: GeomPoint X=322.073 Y=-91.7794 Z=0
    g273: GeomPoint X=318.073 Y=-87.7794 Z=0
    g274: LineSegment StartX=362.567 StartY=-89.8542 StartZ=0 EndX=321.579 EndY=-67.3492 EndZ=0
    g275: LineSegment StartX=318.073 StartY=-69.424 StartZ=0 EndX=318.073 EndY=-87.7794 EndZ=0
    g276: LineSegment StartX=322.073 StartY=-91.7794 StartZ=0 EndX=362.073 EndY=-91.7794 EndZ=0
    g277: Circle CenterX=2.07281 CenterY=124.221 CenterZ=0 NormalX=0 NormalY=0 NormalZ=1 AngleXU=0 Radius=1
    g278: Circle CenterX=1.57905 CenterY=122.295 CenterZ=0 NormalX=0 NormalY=0 NormalZ=1 AngleXU=0 Radius=1
    g279: BSplineCurve PolesCount=3 KnotsCount=2 Degree=2 IsPeriodic=0
    g280: GeomPoint X=2.07281 Y=124.221 Z=0
    g281: GeomPoint X=1.57905 Y=122.295 Z=0
    g282: Circle CenterX=42.0728 CenterY=124.221 CenterZ=0 NormalX=0 NormalY=0 NormalZ=1 AngleXU=0 Radius=1
    g283: Circle CenterX=46.0728 CenterY=124.221 CenterZ=0 NormalX=0 NormalY=0 NormalZ=1 AngleXU=0 Radius=1
    g284: Circle CenterX=46.0728 CenterY=120.221 CenterZ=0 NormalX=0 NormalY=0 NormalZ=1 AngleXU=0 Radius=1
    g285: BSplineCurve PolesCount=3 KnotsCount=2 Degree=2 IsPeriodic=0
    g286: GeomPoint X=42.0728 Y=124.221 Z=0
    g287: GeomPoint X=46.0728 Y=120.221 Z=0
    g288: Circle CenterX=46.0728 CenterY=109.865 CenterZ=0 NormalX=0 NormalY=0 NormalZ=1 AngleXU=0 Radius=1
    g289: Circle CenterX=46.0728 CenterY=105.865 CenterZ=0 NormalX=0 NormalY=0 NormalZ=1 AngleXU=0 Radius=1
    g290: Circle CenterX=42.0728 CenterY=105.865 CenterZ=0 NormalX=0 NormalY=0 NormalZ=1 AngleXU=0 Radius=1
    g291: BSplineCurve PolesCount=3 KnotsCount=2 Degree=2 IsPeriodic=0
    g292: GeomPoint X=46.0728 Y=109.865 Z=0
    g293: GeomPoint X=42.0728 Y=105.865 Z=0
    g294: Circle CenterX=35.5028 CenterY=105.865 CenterZ=0 NormalX=0 NormalY=0 NormalZ=1 AngleXU=0 Radius=1
    g295: Circle CenterX=31.5028 CenterY=105.865 CenterZ=0 NormalX=0 NormalY=0 NormalZ=1 AngleXU=0 Radius=1
    g296: Circle CenterX=27.9965 CenterY=107.79 CenterZ=0 NormalX=0 NormalY=0 NormalZ=1 AngleXU=0 Radius=1
    g297: BSplineCurve PolesCount=3 KnotsCount=2 Degree=2 IsPeriodic=0
    g298: GeomPoint X=35.5028 Y=105.865 Z=0
    g299: GeomPoint X=27.9965 Y=107.79 Z=0
    g300: LineSegment StartX=2.07281 StartY=124.221 StartZ=0 EndX=42.0728 EndY=124.221 EndZ=0
    g301: LineSegment StartX=46.0728 StartY=120.221 StartZ=0 EndX=46.0728 EndY=109.865 EndZ=0
    g302: LineSegment StartX=42.0728 StartY=105.865 StartZ=0 EndX=35.5028 EndY=105.865 EndZ=0
    g303: LineSegment StartX=27.9965 StartY=107.79 StartZ=0 EndX=1.57905 EndY=122.295 EndZ=0
    g304: Circle CenterX=42.5666 CenterY=-67.3492 CenterZ=0 NormalX=0 NormalY=0 NormalZ=1 AngleXU=0 Radius=1
    g305: Circle CenterX=46.0728 CenterY=-65.424 CenterZ=0 NormalX=0 NormalY=0 NormalZ=1 AngleXU=0 Radius=1
    g306: Circle CenterX=46.0728 CenterY=-69.424 CenterZ=0 NormalX=0 NormalY=0 NormalZ=1 AngleXU=0 Radius=1
    g307: BSplineCurve PolesCount=3 KnotsCount=2 Degree=2 IsPeriodic=0
    g308: GeomPoint X=42.5666 Y=-67.3492 Z=0
    g309: GeomPoint X=46.0728 Y=-69.424 Z=0
    g310: Circle CenterX=46.0728 CenterY=-87.7794 CenterZ=0 NormalX=0 NormalY=0 NormalZ=1 AngleXU=0 Radius=1
    g311: Circle CenterX=46.0728 CenterY=-91.7794 CenterZ=0 NormalX=0 NormalY=0 NormalZ=1 AngleXU=0 Radius=1
    g312: Circle CenterX=42.0728 CenterY=-91.7794 CenterZ=0 NormalX=0 NormalY=0 NormalZ=1 AngleXU=0 Radius=1
    g313: BSplineCurve PolesCount=3 KnotsCount=2 Degree=2 IsPeriodic=0
    g314: GeomPoint X=46.0728 Y=-87.7794 Z=0
    g315: GeomPoint X=42.0728 Y=-91.7794 Z=0
    g316: Circle CenterX=2.07281 CenterY=-91.7794 CenterZ=0 NormalX=0 NormalY=0 NormalZ=1 AngleXU=0 Radius=1
    g317: Circle CenterX=-1.92719 CenterY=-91.7794 CenterZ=0 NormalX=0 NormalY=0 NormalZ=1 AngleXU=0 Radius=1
    g318: Circle CenterX=1.57905 CenterY=-89.8542 CenterZ=0 NormalX=0 NormalY=0 NormalZ=1 AngleXU=0 Radius=1
    g319: BSplineCurve PolesCount=3 KnotsCount=2 Degree=2 IsPeriodic=0
    g320: GeomPoint X=2.07281 Y=-91.7794 Z=0
    g321: GeomPoint X=1.57905 Y=-89.8542 Z=0
    g322: LineSegment StartX=2.07281 StartY=-91.7794 StartZ=0 EndX=42.0728 EndY=-91.7794 EndZ=0
    g323: LineSegment StartX=46.0728 StartY=-87.7794 StartZ=0 EndX=46.0728 EndY=-69.424 EndZ=0
    g324: LineSegment StartX=42.5666 StartY=-67.3492 StartZ=0 EndX=1.57905 EndY=-89.8542 EndZ=0
    g325: Circle CenterX=322.073 CenterY=76.4095 CenterZ=0 NormalX=0 NormalY=0 NormalZ=1 AngleXU=0 Radius=4
    g326: BSplineCurve PolesCount=3 KnotsCount=2 Degree=2 IsPeriodic=0
    g327: GeomPoint X=318.073 Y=72.4095 Z=0
    g328: GeomPoint X=322.073 Y=76.4095 Z=0
    g329: Circle CenterX=375.073 CenterY=72.4095 CenterZ=0 NormalX=0 NormalY=0 NormalZ=1 AngleXU=0 Radius=1
    g330: Circle CenterX=375.073 CenterY=76.4095 CenterZ=0 NormalX=0 NormalY=0 NormalZ=1 AngleXU=0 Radius=1
    g331: Circle CenterX=371.073 CenterY=76.4095 CenterZ=0 NormalX=0 NormalY=0 NormalZ=1 AngleXU=0 Radius=1
    g332: BSplineCurve PolesCount=3 KnotsCount=2 Degree=2 IsPeriodic=0
    g333: GeomPoint X=375.073 Y=72.4095 Z=0
    g334: GeomPoint X=371.073 Y=76.4095 Z=0
    g335: LineSegment StartX=322.073 StartY=76.4095 StartZ=0 EndX=371.073 EndY=76.4095 EndZ=0
    g336: LineSegment StartX=318.073 StartY=72.4095 StartZ=0 EndX=318.073 EndY=-47.4805 EndZ=0
    g337: LineSegment StartX=375.073 StartY=72.4095 StartZ=0 EndX=375.073 EndY=-78.7896 EndZ=0
    g338: ArcOfCircle CenterX=-26.9272 CenterY=22.1087 CenterZ=0 NormalX=0 NormalY=0 NormalZ=1 AngleXU=0 Radius=4 StartAngle=5e-16 EndAngle=3.14159
    g339: LineSegment StartX=-22.9272 StartY=22.1087 StartZ=0 EndX=-18.9272 EndY=-83.7794 EndZ=0
    g340: LineSegment StartX=-34.9272 StartY=-83.7794 StartZ=0 EndX=-30.9272 EndY=22.1087 EndZ=0
    g341: ArcOfCircle CenterX=391.073 CenterY=22.1087 CenterZ=0 NormalX=0 NormalY=0 NormalZ=1 AngleXU=0 Radius=4 StartAngle=0 EndAngle=3.14159
    g342: LineSegment StartX=387.073 StartY=22.1087 StartZ=0 EndX=383.073 EndY=-83.7794 EndZ=0
    g343: LineSegment StartX=395.073 StartY=22.1087 StartZ=0 EndX=399.073 EndY=-83.7794 EndZ=0
    g344: Circle CenterX=-10.9272 CenterY=-78.7794 CenterZ=0 NormalX=0 NormalY=0 NormalZ=1 AngleXU=0 Radius=1
    g345: Circle CenterX=-10.9272 CenterY=-82.7794 CenterZ=0 NormalX=0 NormalY=0 NormalZ=1 AngleXU=0 Radius=1
    g346: Circle CenterX=-7.42095 CenterY=-80.8542 CenterZ=0 NormalX=0 NormalY=0 NormalZ=1 AngleXU=0 Radius=1
    g347: BSplineCurve PolesCount=3 KnotsCount=2 Degree=2 IsPeriodic=0
    g348: GeomPoint X=-10.9272 Y=-78.7794 Z=0
    g349: GeomPoint X=-7.42095 Y=-80.8542 Z=0
    g350: Circle CenterX=42.5666 CenterY=-53.4075 CenterZ=0 NormalX=0 NormalY=0 NormalZ=1 AngleXU=0 Radius=1
    g351: Circle CenterX=46.0728 CenterY=-51.4823 CenterZ=0 NormalX=0 NormalY=0 NormalZ=1 AngleXU=0 Radius=1
    g352: Circle CenterX=46.0728 CenterY=-47.4823 CenterZ=0 NormalX=0 NormalY=0 NormalZ=1 AngleXU=0 Radius=1
    g353: BSplineCurve PolesCount=3 KnotsCount=2 Degree=2 IsPeriodic=0
    g354: GeomPoint X=42.5666 Y=-53.4075 Z=0
    g355: GeomPoint X=46.0728 Y=-47.4823 Z=0
    g356: Circle CenterX=46.0728 CenterY=72.4095 CenterZ=0 NormalX=0 NormalY=0 NormalZ=1 AngleXU=0 Radius=1
    g357: Circle CenterX=46.0728 CenterY=76.4095 CenterZ=0 NormalX=0 NormalY=0 NormalZ=1 AngleXU=0 Radius=1
    g358: Circle CenterX=42.0728 CenterY=76.4095 CenterZ=0 NormalX=0 NormalY=0 NormalZ=1 AngleXU=0 Radius=1
    g359: BSplineCurve PolesCount=3 KnotsCount=2 Degree=2 IsPeriodic=0
    g360: GeomPoint X=46.0728 Y=72.4095 Z=0
    g361: GeomPoint X=42.0728 Y=76.4095 Z=0
    g362: Circle CenterX=-6.92718 CenterY=76.4095 CenterZ=0 NormalX=0 NormalY=0 NormalZ=1 AngleXU=0 Radius=1
    g363: Circle CenterX=-10.9272 CenterY=76.4095 CenterZ=0 NormalX=0 NormalY=0 NormalZ=1 AngleXU=0 Radius=1
    g364: Circle CenterX=-10.9272 CenterY=72.4095 CenterZ=0 NormalX=0 NormalY=0 NormalZ=1 AngleXU=0 Radius=1
    g365: BSplineCurve PolesCount=3 KnotsCount=2 Degree=2 IsPeriodic=0
    g366: GeomPoint X=-6.92718 Y=76.4095 Z=0
    g367: GeomPoint X=-10.9272 Y=72.4095 Z=0
    g368: LineSegment StartX=-10.9272 StartY=72.4095 StartZ=0 EndX=-10.9272 EndY=-78.7794 EndZ=0
    g369: LineSegment StartX=-7.42095 StartY=-80.8542 StartZ=0 EndX=42.5666 EndY=-53.4075 EndZ=0
    g370: LineSegment StartX=46.0728 StartY=-47.4823 StartZ=0 EndX=46.0728 EndY=72.4095 EndZ=0
    g371: LineSegment StartX=42.0728 StartY=76.4095 StartZ=0 EndX=-6.92719 EndY=76.4095 EndZ=0
    g372: LineSegment StartX=232.072 StartY=136.221 StartZ=0 EndX=232.072 EndY=-117.815 EndZ=0
    g373: LineSegment StartX=132.072 StartY=136.221 StartZ=0 EndX=132.072 EndY=-121.309 EndZ=0
    g374: LineSegment StartX=245.072 StartY=136.221 StartZ=0 EndX=245.072 EndY=-116.499 EndZ=0
    g375: LineSegment StartX=119.072 StartY=136.221 StartZ=0 EndX=119.072 EndY=-116.228 EndZ=0
    g376: LineSegment StartX=-42.9272 StartY=136.221 StartZ=0 EndX=407.073 EndY=136.221 EndZ=0
    g377: LineSegment StartX=232.072 StartY=136.221 StartZ=0 EndX=220.072 EndY=136.221 EndZ=0
    g378: LineSegment StartX=232.072 StartY=136.221 StartZ=0 EndX=232.072 EndY=124.221 EndZ=0
    g379: LineSegment StartX=220.072 StartY=136.221 StartZ=0 EndX=220.072 EndY=124.221 EndZ=0
    g380: LineSegment StartX=220.011 StartY=122.701 StartZ=0 EndX=226.011 EndY=122.701 EndZ=0
    g381: LineSegment StartX=220.072 StartY=136.221 StartZ=0 EndX=226.072 EndY=136.221 EndZ=0
    g382: LineSegment StartX=220.072 StartY=136.221 StartZ=0 EndX=220.072 EndY=130.221 EndZ=0
  constraints (641):
    c: Vertical(g0)
    c: Vertical(g1)
    c: Block(g1)
    c: Block(g0)
    c: Weight(g4) = 1
    c: Equal(g4,g5)
    c: Equal(g4,g6)
    c: InternalAlignment(g4,g7)
    c: InternalAlignment(g5,g7)
    c: InternalAlignment(g6,g7)
    c: InternalAlignment(g8,g7)
    c: InternalAlignment(g9,g7)
    c: Weight(g10) = 1
    c: Equal(g10,g11)
    c: Equal(g10,g12)
    c: InternalAlignment(g10,g13)
    c: InternalAlignment(g11,g13)
    c: InternalAlignment(g12,g13)
    c: InternalAlignment(g14,g13)
    c: InternalAlignment(g15,g13)
    c: Block(g13)
    c: Block(g7)
    c: Weight(g16) = 1
    c: Equal(g16,g17)
    c: Equal(g16,g18)
    c: InternalAlignment(g16,g19)
    c: InternalAlignment(g17,g19)
    c: InternalAlignment(g18,g19)
    c: InternalAlignment(g20,g19)
    c: InternalAlignment(g21,g19)
    c: Weight(g22) = 1
    c: Equal(g22,g23)
    c: Equal(g22,g24)
    c: InternalAlignment(g22,g25)
    c: InternalAlignment(g23,g25)
    c: InternalAlignment(g24,g25)
    c: InternalAlignment(g26,g25)
    c: InternalAlignment(g27,g25)
    c: Block(g25)
    c: Block(g19)
    c: Weight(g28) = 1
    c: Equal(g28,g29)
    c: Equal(g28,g30)
    c: InternalAlignment(g28,g31)
    c: InternalAlignment(g29,g31)
    c: InternalAlignment(g30,g31)
    c: InternalAlignment(g32,g31)
    c: InternalAlignment(g33,g31)
    c: Weight(g34) = 1
    c: Equal(g34,g35)
    c: Equal(g34,g36)
    c: InternalAlignment(g34,g37)
    c: InternalAlignment(g35,g37)
    c: InternalAlignment(g36,g37)
    c: InternalAlignment(g38,g37)
    c: InternalAlignment(g39,g37)
    c: Block(g31)
    c: Block(g37)
    c: Coincident(g40,g1)
    c: Coincident(g40,g0)
    c: Horizontal(g40)
    c: Distance(g40) = 450
    c: Weight(g41) = 1
    c: Equal(g41,g42)
    c: Equal(g41,g43)
    c: InternalAlignment(g41,g44)
    c: InternalAlignment(g42,g44)
    c: InternalAlignment(g43,g44)
    c: InternalAlignment(g45,g44)
    c: InternalAlignment(g46,g44)
    c: Block(g44)
    c: Weight(g47) = 1
    c: Equal(g47,g48)
    c: Equal(g47,g49)
    c: InternalAlignment(g47,g50)
    c: InternalAlignment(g48,g50)
    c: InternalAlignment(g49,g50)
    c: InternalAlignment(g51,g50)
    c: InternalAlignment(g52,g50)
    c: Block(g50)
    c: Weight(g53) = 1
    c: Equal(g53,g54)
    c: Equal(g53,g55)
    c: InternalAlignment(g53,g56)
    c: InternalAlignment(g54,g56)
    c: InternalAlignment(g55,g56)
    c: InternalAlignment(g57,g56)
    c: InternalAlignment(g58,g56)
    c: Block(g56)
    c: Weight(g59) = 1
    c: Equal(g59,g60)
    c: Equal(g59,g61)
    c: InternalAlignment(g59,g62)
    c: InternalAlignment(g60,g62)
    c: InternalAlignment(g61,g62)
    c: InternalAlignment(g63,g62)
    c: InternalAlignment(g64,g62)
    c: Block(g62)
    c: Weight(g65) = 1
    c: Equal(g65,g66)
    c: Equal(g65,g67)
    c: InternalAlignment(g65,g68)
    c: InternalAlignment(g66,g68)
    c: InternalAlignment(g67,g68)
    c: InternalAlignment(g69,g68)
    c: InternalAlignment(g70,g68)
    c: Weight(g71) = 1
    c: Equal(g71,g72)
    c: Equal(g71,g73)
    c: InternalAlignment(g71,g74)
    c: InternalAlignment(g72,g74)
    c: InternalAlignment(g73,g74)
    c: InternalAlignment(g75,g74)
    c: InternalAlignment(g76,g74)
    c: Block(g68)
    c: Block(g74)
    c: Coincident(g77,g68)
    c: Coincident(g77,g74)
    c: Vertical(g77)
    c: Coincident(g78,g68)
    c: Coincident(g78,g50)
    c: Coincident(g79,g50)
    c: Coincident(g79,g74)
    c: Weight(g80) = 1
    c: Equal(g80,g81)
    c: Equal(g80,g82)
    c: InternalAlignment(g80,g83)
    c: InternalAlignment(g81,g83)
    c: InternalAlignment(g82,g83)
    c: InternalAlignment(g84,g83)
    c: InternalAlignment(g85,g83)
    c: Weight(g86) = 1
    c: Equal(g86,g87)
    c: Equal(g86,g88)
    c: InternalAlignment(g86,g89)
    c: InternalAlignment(g87,g89)
    c: InternalAlignment(g88,g89)
    c: InternalAlignment(g90,g89)
    c: InternalAlignment(g91,g89)
    c: Block(g83)
    c: Block(g89)
    c: Coincident(g92,g83)
    c: Coincident(g92,g89)
    c: Vertical(g92)
    c: Coincident(g93,g83)
    c: Coincident(g93,g44)
    c: Coincident(g94,g44)
    c: Coincident(g94,g89)
    c: Weight(g95) = 1
    c: Equal(g95,g96)
    c: Equal(g95,g97)
    c: InternalAlignment(g95,g98)
    c: InternalAlignment(g96,g98)
    c: InternalAlignment(g97,g98)
    c: InternalAlignment(g99,g98)
    c: InternalAlignment(g100,g98)
    c: Weight(g101) = 1
    c: Equal(g101,g102)
    c: Equal(g101,g103)
    c: InternalAlignment(g101,g104)
    c: InternalAlignment(g102,g104)
    c: InternalAlignment(g103,g104)
    c: InternalAlignment(g105,g104)
    c: InternalAlignment(g106,g104)
    c: Block(g98)
    c: Block(g104)
    c: Coincident(g107,g98)
    c: Coincident(g107,g104)
    c: Vertical(g107)
    c: Coincident(g108,g104)
    c: Coincident(g108,g62)
    c: Coincident(g109,g62)
    c: Coincident(g109,g98)
    c: Weight(g110) = 1
    c: Equal(g110,g111)
    c: Equal(g110,g112)
    c: InternalAlignment(g110,g113)
    c: InternalAlignment(g111,g113)
    c: InternalAlignment(g112,g113)
    c: InternalAlignment(g114,g113)
    c: InternalAlignment(g115,g113)
    c: Weight(g116) = 1
    c: Equal(g116,g117)
    c: Equal(g116,g118)
    c: InternalAlignment(g116,g119)
    c: InternalAlignment(g117,g119)
    c: InternalAlignment(g118,g119)
    c: InternalAlignment(g120,g119)
    c: InternalAlignment(g121,g119)
    c: Block(g113)
    c: Block(g119)
    c: Coincident(g122,g113)
    c: Coincident(g122,g119)
    c: Vertical(g122)
    c: Coincident(g123,g119)
    c: Coincident(g123,g56)
    c: Coincident(g124,g56)
    c: Coincident(g124,g113)
    c: Weight(g125) = 1
    c: Equal(g125,g126)
    c: Equal(g125,g127)
    c: InternalAlignment(g125,g128)
    c: InternalAlignment(g126,g128)
    c: InternalAlignment(g127,g128)
    c: InternalAlignment(g129,g128)
    c: InternalAlignment(g130,g128)
    c: Weight(g131) = 1
    c: Equal(g131,g132)
    c: Equal(g131,g133)
    c: InternalAlignment(g131,g134)
    c: InternalAlignment(g132,g134)
    c: InternalAlignment(g133,g134)
    c: InternalAlignment(g135,g134)
    c: InternalAlignment(g136,g134)
    c: Weight(g137) = 1
    c: Equal(g137,g138)
    c: Equal(g137,g139)
    c: InternalAlignment(g137,g140)
    c: InternalAlignment(g138,g140)
    c: InternalAlignment(g139,g140)
    c: InternalAlignment(g141,g140)
    c: InternalAlignment(g142,g140)
    c: Weight(g143) = 1
    c: Equal(g143,g144)
    c: Equal(g143,g145)
    c: InternalAlignment(g143,g146)
    c: InternalAlignment(g144,g146)
    c: InternalAlignment(g145,g146)
    c: InternalAlignment(g147,g146)
    c: InternalAlignment(g148,g146)
    c: Block(g146)
    c: Block(g140)
    c: Block(g134)
    c: Block(g128)
    c: Coincident(g149,g25)
    c: Coincident(g149,g146)
    c: Coincident(g150,g146)
    c: Coincident(g150,g140)
    c: Horizontal(g150)
    c: Coincident(g151,g140)
    c: Coincident(g151,g25)
    c: Vertical(g151)
    c: Coincident(g152,g19)
    c: Coincident(g152,g134)
    c: Vertical(g152)
    c: Coincident(g153,g134)
    c: Coincident(g153,g128)
    c: Horizontal(g153)
    c: Coincident(g154,g128)
    c: Coincident(g154,g19)
    c: Weight(g155) = 1
    c: Equal(g155,g156)
    c: Equal(g155,g157)
    c: InternalAlignment(g155,g158)
    c: InternalAlignment(g156,g158)
    c: InternalAlignment(g157,g158)
    c: InternalAlignment(g159,g158)
    c: InternalAlignment(g160,g158)
    c: Weight(g161) = 1
    c: Equal(g161,g162)
    c: Equal(g161,g163)
    c: InternalAlignment(g161,g164)
    c: InternalAlignment(g162,g164)
    c: InternalAlignment(g163,g164)
    c: InternalAlignment(g165,g164)
    c: InternalAlignment(g166,g164)
    c: Weight(g167) = 1
    c: Equal(g167,g168)
    c: Equal(g167,g169)
    c: InternalAlignment(g167,g170)
    c: InternalAlignment(g168,g170)
    c: InternalAlignment(g169,g170)
    c: InternalAlignment(g171,g170)
    c: InternalAlignment(g172,g170)
    c: Weight(g173) = 1
    c: Equal(g173,g174)
    c: Equal(g173,g175)
    c: InternalAlignment(g173,g176)
    c: InternalAlignment(g174,g176)
    c: InternalAlignment(g175,g176)
    c: InternalAlignment(g177,g176)
    c: InternalAlignment(g178,g176)
    c: Block(g176)
    c: Block(g170)
    c: Block(g164)
    c: Block(g158)
    c: Coincident(g179,g176)
    c: Coincident(g179,g170)
    c: Horizontal(g179)
    c: Coincident(g180,g170)
    c: Coincident(g180,g7)
    c: Vertical(g180)
    c: Coincident(g181,g13)
    c: Coincident(g181,g164)
    c: Vertical(g181)
    c: Coincident(g182,g164)
    c: Coincident(g182,g158)
    c: Horizontal(g182)
    c: Coincident(g183,g158)
    c: Coincident(g183,g13)
    c: Coincident(g184,g7)
    c: Weight(g185) = 1
    c: Equal(g185,g186)
    c: Equal(g185,g187)
    c: InternalAlignment(g185,g188)
    c: InternalAlignment(g186,g188)
    c: InternalAlignment(g187,g188)
    c: InternalAlignment(g189,g188)
    c: InternalAlignment(g190,g188)
    c: Weight(g191) = 1
    c: Equal(g191,g192)
    c: Equal(g191,g193)
    c: InternalAlignment(g191,g194)
    c: InternalAlignment(g192,g194)
    c: InternalAlignment(g193,g194)
    c: InternalAlignment(g195,g194)
    c: InternalAlignment(g196,g194)
    c: Block(g194)
    c: Block(g188)
    c: Coincident(g197,g194)
    c: Coincident(g197,g31)
    c: Coincident(g198,g31)
    c: Coincident(g198,g188)
    c: Coincident(g199,g188)
    c: Coincident(g199,g194)
    c: Vertical(g199)
    c: Weight(g200) = 1
    c: Equal(g200,g201)
    c: Equal(g200,g202)
    c: InternalAlignment(g200,g203)
    c: InternalAlignment(g201,g203)
    c: InternalAlignment(g202,g203)
    c: InternalAlignment(g204,g203)
    c: InternalAlignment(g205,g203)
    c: Weight(g206) = 1
    c: Equal(g206,g207)
    c: Equal(g206,g208)
    c: InternalAlignment(g206,g209)
    c: InternalAlignment(g207,g209)
    c: InternalAlignment(g208,g209)
    c: InternalAlignment(g210,g209)
    c: InternalAlignment(g211,g209)
    c: Block(g209)
    c: Block(g203)
    c: Coincident(g212,g203)
    c: Coincident(g212,g37)
    c: Coincident(g213,g37)
    c: Coincident(g213,g209)
    c: Coincident(g214,g209)
    c: Coincident(g214,g203)
    c: Vertical(g214)
    c: Horizontal(g215)
    c: Block(g215)
    c: Vertical(g216)
    c: Block(g216)
    c: Block(g217)
    c: Weight(g218) = 1
    c: Equal(g218,g219)
    c: Equal(g218,g220)
    c: InternalAlignment(g218,g221)
    c: InternalAlignment(g219,g221)
    c: InternalAlignment(g220,g221)
    c: InternalAlignment(g222,g221)
    c: InternalAlignment(g223,g221)
    c: Weight(g224) = 1
    c: Equal(g224,g225)
    c: Equal(g224,g226)
    c: InternalAlignment(g224,g227)
    c: InternalAlignment(g225,g227)
    c: InternalAlignment(g226,g227)
    c: InternalAlignment(g228,g227)
    c: InternalAlignment(g229,g227)
    c: Weight(g230) = 1
    c: Equal(g230,g231)
    c: Equal(g230,g232)
    c: InternalAlignment(g230,g233)
    c: InternalAlignment(g231,g233)
    c: InternalAlignment(g232,g233)
    c: InternalAlignment(g234,g233)
    c: InternalAlignment(g235,g233)
    c: Weight(g236) = 1
    c: Equal(g236,g237)
    c: Equal(g236,g238)
    c: InternalAlignment(g236,g239)
    c: InternalAlignment(g237,g239)
    c: InternalAlignment(g238,g239)
    c: InternalAlignment(g240,g239)
    c: InternalAlignment(g241,g239)
    c: Block(g221)
    c: Block(g227)
    c: Block(g233)
    c: Block(g239)
    c: Coincident(g242,g227)
    c: Coincident(g242,g221)
    c: Horizontal(g242)
    c: Block(g184)
    c: Weight(g243) = 1
    c: Equal(g243,g244)
    c: Equal(g243,g245)
    c: InternalAlignment(g243,g246)
    c: InternalAlignment(g244,g246)
    c: InternalAlignment(g245,g246)
    c: InternalAlignment(g247,g246)
    c: InternalAlignment(g248,g246)
    c: Weight(g249) = 1
    c: Equal(g249,g250)
    c: Equal(g249,g251)
    c: InternalAlignment(g249,g252)
    c: InternalAlignment(g250,g252)
    c: InternalAlignment(g251,g252)
    c: InternalAlignment(g253,g252)
    c: InternalAlignment(g254,g252)
    c: Block(g246)
    c: Block(g252)
    c: Coincident(g255,g246)
    c: Coincident(g255,g252)
    c: Weight(g256) = 1
    c: Equal(g256,g257)
    c: Equal(g256,g258)
    c: InternalAlignment(g256,g259)
    c: InternalAlignment(g257,g259)
    c: InternalAlignment(g258,g259)
    c: InternalAlignment(g260,g259)
    c: InternalAlignment(g261,g259)
    c: Weight(g262) = 1
    c: Equal(g262,g263)
    c: Equal(g262,g264)
    c: InternalAlignment(g262,g265)
    c: InternalAlignment(g263,g265)
    c: InternalAlignment(g264,g265)
    c: InternalAlignment(g266,g265)
    c: InternalAlignment(g267,g265)
    c: Weight(g268) = 1
    c: Equal(g268,g269)
    c: Equal(g268,g270)
    c: InternalAlignment(g268,g271)
    c: InternalAlignment(g269,g271)
    c: InternalAlignment(g270,g271)
    c: InternalAlignment(g272,g271)
    c: InternalAlignment(g273,g271)
    c: Block(g271)
    c: Block(g265)
    c: Block(g259)
    c: Coincident(g274,g265)
    c: Coincident(g274,g259)
    c: Coincident(g275,g259)
    c: Coincident(g275,g271)
    c: Vertical(g275)
    c: Coincident(g276,g271)
    c: Coincident(g276,g265)
    c: Horizontal(g276)
    c: Weight(g277) = 1
    c: Equal(g277,g278)
    c: InternalAlignment(g277,g279)
    c: InternalAlignment(g278,g279)
    c: InternalAlignment(g280,g279)
    c: InternalAlignment(g281,g279)
    c: Weight(g282) = 1
    c: InternalAlignment(g283,g285)
    c: InternalAlignment(g284,g285)
    c: InternalAlignment(g286,g285)
    c: InternalAlignment(g287,g285)
    c: Weight(g288) = 1
    c: Equal(g288,g289)
    c: Equal(g288,g290)
    c: InternalAlignment(g288,g291)
    c: InternalAlignment(g289,g291)
    c: InternalAlignment(g290,g291)
    c: InternalAlignment(g292,g291)
    c: InternalAlignment(g293,g291)
    c: Equal(g294,g295)
    c: Equal(g294,g296)
    c: InternalAlignment(g294,g297)
    c: InternalAlignment(g295,g297)
    c: InternalAlignment(g296,g297)
    c: InternalAlignment(g298,g297)
    c: InternalAlignment(g299,g297)
    c: Block(g285)
    c: Block(g291)
    c: Block(g297)
    c: Block(g279)
    c: Coincident(g300,g279)
    c: Coincident(g300,g285)
    c: Horizontal(g300)
    c: Coincident(g301,g285)
    c: Coincident(g301,g291)
    c: Vertical(g301)
    c: Coincident(g302,g291)
    c: Coincident(g302,g297)
    c: Horizontal(g302)
    c: Coincident(g303,g297)
    c: Coincident(g303,g279)
    c: Weight(g304) = 1
    c: Equal(g304,g305)
    c: Equal(g304,g306)
    c: InternalAlignment(g304,g307)
    c: InternalAlignment(g305,g307)
    c: InternalAlignment(g306,g307)
    c: InternalAlignment(g308,g307)
    c: InternalAlignment(g309,g307)
    c: Weight(g310) = 1
    c: Equal(g310,g311)
    c: Equal(g310,g312)
    c: InternalAlignment(g310,g313)
    c: InternalAlignment(g311,g313)
    c: InternalAlignment(g312,g313)
    c: InternalAlignment(g314,g313)
    c: InternalAlignment(g315,g313)
    c: Weight(g316) = 1
    c: Equal(g316,g317)
    c: Equal(g316,g318)
    c: InternalAlignment(g316,g319)
    c: InternalAlignment(g317,g319)
    c: InternalAlignment(g318,g319)
    c: InternalAlignment(g320,g319)
    c: InternalAlignment(g321,g319)
    c: Block(g319)
    c: Block(g313)
    c: Block(g307)
    c: Coincident(g322,g319)
    c: Coincident(g322,g313)
    c: Horizontal(g322)
    c: Coincident(g323,g313)
    c: Coincident(g323,g307)
    c: Vertical(g323)
    c: Coincident(g324,g307)
    c: Coincident(g324,g319)
    c: InternalAlignment(g325,g326)
    c: InternalAlignment(g327,g326)
    c: InternalAlignment(g328,g326)
    c: Block(g326)
    c: Equal(g329,g330)
    c: Equal(g329,g331)
    c: InternalAlignment(g329,g332)
    c: InternalAlignment(g330,g332)
    c: InternalAlignment(g331,g332)
    c: InternalAlignment(g333,g332)
    c: InternalAlignment(g334,g332)
    c: Block(g332)
    c: Coincident(g335,g326)
    c: Horizontal(g335)
    c: Block(g335)
    c: Coincident(g336,g326)
    c: Coincident(g336,g252)
    c: Vertical(g336)
    c: Coincident(g337,g332)
    c: Coincident(g337,g246)
    c: Vertical(g337)
    c: Block(g338)
    c: Block(g2)
    c: Distance(g336) = 119.89
    c: Coincident(g339,g338)
    c: Coincident(g339,g2)
    c: Coincident(g340,g2)
    c: Coincident(g340,g338)
    c: Block(g3)
    c: Block(g341)
    c: Coincident(g342,g341)
    c: Coincident(g342,g3)
    c: Coincident(g343,g341)
    c: Coincident(g343,g3)
    c: Block(g343)
    c: Block(g342)
    c: Weight(g344) = 1
    c: Equal(g344,g345)
    c: Equal(g344,g346)
    c: InternalAlignment(g344,g347)
    c: InternalAlignment(g345,g347)
    c: InternalAlignment(g346,g347)
    c: InternalAlignment(g348,g347)
    c: InternalAlignment(g349,g347)
    c: Weight(g350) = 1
    c: Equal(g350,g351)
    c: Equal(g350,g352)
    c: InternalAlignment(g350,g353)
    c: InternalAlignment(g351,g353)
    c: InternalAlignment(g352,g353)
    c: InternalAlignment(g354,g353)
    c: InternalAlignment(g355,g353)
    c: Weight(g356) = 1
    c: Equal(g356,g357)
    c: Equal(g356,g358)
    c: InternalAlignment(g356,g359)
    c: InternalAlignment(g357,g359)
    c: InternalAlignment(g358,g359)
    c: InternalAlignment(g360,g359)
    c: InternalAlignment(g361,g359)
    c: Weight(g362) = 1
    c: Equal(g362,g363)
    c: Equal(g362,g364)
    c: InternalAlignment(g362,g365)
    c: InternalAlignment(g363,g365)
    c: InternalAlignment(g364,g365)
    c: InternalAlignment(g366,g365)
    c: InternalAlignment(g367,g365)
    c: Block(g365)
    c: Block(g359)
    c: Block(g353)
    c: Block(g347)
    c: Coincident(g368,g365)
    c: Coincident(g368,g347)
    c: Vertical(g368)
    c: Coincident(g369,g347)
    c: Coincident(g369,g353)
    c: Coincident(g370,g353)
    c: Coincident(g370,g359)
    c: Vertical(g370)
    c: Coincident(g371,g359)
    c: Coincident(g371,g365)
    c: Horizontal(g371)
    c: Vertical(g372)
    c: Vertical(g373)
    c: Vertical(g374)
    c: Vertical(g375)
    c: Coincident(g376,g0)
    c: Coincident(g376,g1)
    c: Horizontal(g376)
    c: Block(g376)
    c: Distance(g376) = 450
    c: Block(g374)
    c: Block(g372)
    c: Block(g373)
    c: Block(g375)
    c: Distance(g0) = 240
    c: Horizontal(g377)
    c: Distance(g377) = 12
    c: Coincident(g377,g372)
    c: Vertical(g378)
    c: Distance(g378) = 12
    c: Coincident(g378,g372)
    c: Coincident(g379,g377)
    c: Vertical(g379)
    c: PointOnObject(g379,g182)
    c: Horizontal(g380)
    c: Distance(g380) = 6
    c: Horizontal(g381)
    c: Equal(g380,g381) = 6
    c: Vertical(g382)
    c: Distance(g382) = 6
    c: Coincident(g382,g377)
    c: Coincident(g381,g377)
FEATURE [Part::Extrusion] Extrude005
  Base = -> Sketch003
  Dir = (0,0,1)
  DirMode = 2
  FaceMakerClass = Part::FaceMakerBullseye
  LengthFwd = 24
  LengthRev = 0
  Solid = true
  Symmetric = false
